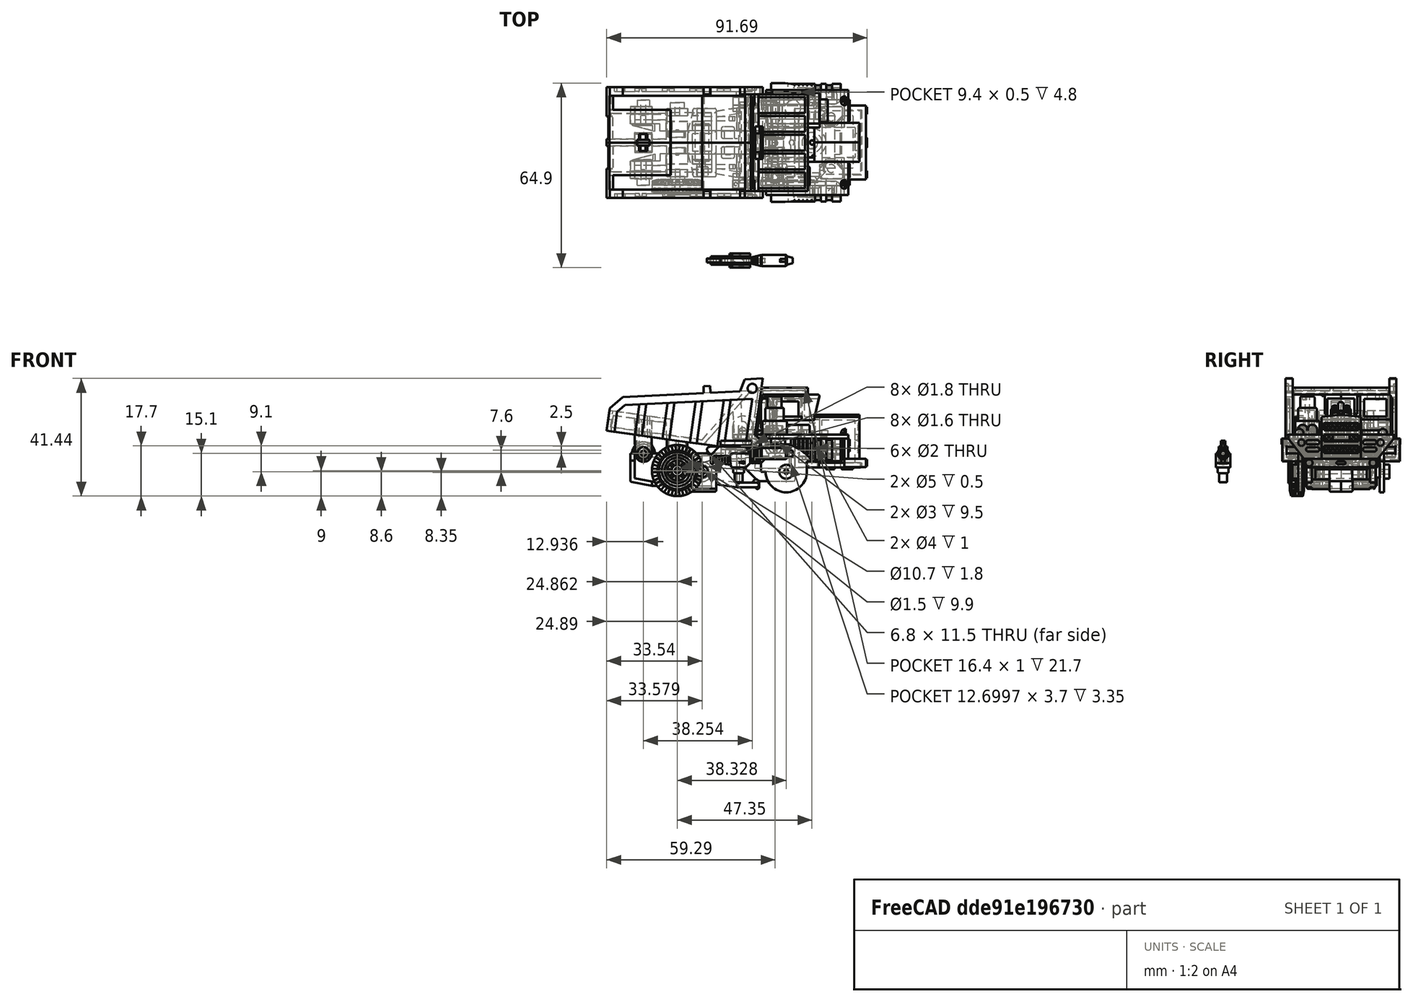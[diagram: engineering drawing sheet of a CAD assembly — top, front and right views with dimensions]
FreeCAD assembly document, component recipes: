
FREECAD ASSEMBLY — COMPONENT RECIPES ("Longhaul")

This assembly document has 21 components, labeled P0..P20 below (a component is one placed body or linked part). 19 of them carry a construction recipe — the FreeCAD feature program that regenerates the part from scratch, quoted from this document or its linked companion documents; the rest are supplied as boundary geometry only. No exploded tour is included for this assembly.
NOTE — document 4 of 4 of this assembly tour. The two overview renders and the header above are repeated from document 1; the component sections below continue where the previous document stopped.
COMPONENT P15 — recipe-attached ("Tire2", modeled in this document).
Construction recipe (the document's own serialized feature program — sketch geometry with constraints, then the solid features built on it; lengths are millimeters unless a unit is written):

FEATURE [Sketcher::SketchObject] Sketch235
  ArcFitTolerance = 1e-06
  AttachmentSupport = -> [XZ_Plane007]
  FullyConstrained = true
  MakeInternals = false
  MapMode = 5
  Placement = pos=(0,0,0) rot=(1,0,0;1.5708rad)
  sketch-geometry (1):
    g0: Circle CenterX=0 CenterY=0 CenterZ=0 NormalX=0 NormalY=0 NormalZ=1 AngleXU=0 Radius=4.5
  constraints (2):
    c: Coincident(g0,g-1)
    c: Diameter(g0) = 9
FEATURE [PartDesign::Pad] Pad145
  Direction = (0,-1,2e-16)
  Length = 5.5
  Length2 = 10
  Placement = pos=(0,0,0) rot=(1,0,0;1.5708rad)
  Profile = -> Sketch235
  ReferenceAxis = -> Sketch235 [N_Axis]
  Refine = true
  Suppressed = false
  Type = 0
FEATURE [Sketcher::SketchObject] Sketch236
  ArcFitTolerance = 1e-06
  AttachmentSupport = -> [Pad145]
  FullyConstrained = true
  MakeInternals = false
  MapMode = 5
  Placement = pos=(0,-5.5,0) rot=(1,0,0;1.5708rad)
  sketch-geometry (1):
    g0: Circle CenterX=0 CenterY=0 CenterZ=0 NormalX=0 NormalY=0 NormalZ=1 AngleXU=0 Radius=3.5
  constraints (2):
    c: Coincident(g0,g-1)
    c: Diameter(g0) = 7
FEATURE [PartDesign::Pocket] Pocket097
  BaseFeature = -> Pad145
  Direction = (0,1,-2e-16)
  Length = 0.5
  Length2 = 5
  Placement = pos=(0,0,0) rot=(1,0,0;1.5708rad)
  Profile = -> Sketch236
  ReferenceAxis = -> Sketch236 [N_Axis]
  Refine = true
  Suppressed = false
  Type = 0
FEATURE [Sketcher::SketchObject] Sketch237
  ArcFitTolerance = 1e-06
  AttachmentSupport = -> [Pocket097]
  FullyConstrained = true
  MakeInternals = false
  MapMode = 5
  Placement = pos=(0,-5,1.5e-15) rot=(1,0,0;1.5708rad)
  sketch-geometry (1):
    g0: Circle CenterX=0 CenterY=0 CenterZ=0 NormalX=0 NormalY=0 NormalZ=1 AngleXU=0 Radius=0.75
  constraints (2):
    c: Coincident(g0,g-1)
    c: Diameter(g0) = 1.5
FEATURE [PartDesign::Pocket] Pocket098
  BaseFeature = -> Pocket097
  Direction = (0,1,-2e-16)
  Length = 5
  Length2 = 5
  Placement = pos=(0,0,0) rot=(1,0,0;1.5708rad)
  Profile = -> Sketch237
  ReferenceAxis = -> Sketch237 [N_Axis]
  Refine = true
  Suppressed = false
  Type = 0
FEATURE [Sketcher::SketchObject] Sketch238
  ArcFitTolerance = 1e-06
  AttachmentSupport = -> [Pocket098]
  FullyConstrained = true
  MakeInternals = false
  MapMode = 5
  Placement = pos=(0,-5,1.5e-15) rot=(1,0,0;1.5708rad)
  sketch-geometry (1):
    g0: Circle CenterX=0 CenterY=0 CenterZ=0 NormalX=0 NormalY=0 NormalZ=1 AngleXU=0 Radius=2
  constraints (2):
    c: Coincident(g0,g-1)
    c: Diameter(g0) = 4
FEATURE [PartDesign::Pocket] Pocket099
  BaseFeature = -> Pocket098
  Direction = (0,1,-2e-16)
  Length = 1.5
  Length2 = 5
  Placement = pos=(0,0,0) rot=(1,0,0;1.5708rad)
  Profile = -> Sketch238
  ReferenceAxis = -> Sketch238 [N_Axis]
  Refine = true
  Suppressed = false
  Type = 0
FEATURE [Sketcher::SketchObject] Sketch239
  ArcFitTolerance = 1e-06
  AttachmentSupport = -> [Pocket099]
  FullyConstrained = true
  MakeInternals = false
  MapMode = 5
  Placement = pos=(0,-5,1.5e-15) rot=(1,0,0;1.5708rad)
  sketch-geometry (12):
    g0: Circle CenterX=0 CenterY=2.75 CenterZ=0 NormalX=0 NormalY=0 NormalZ=1 AngleXU=0 Radius=0.5
    g1: Circle CenterX=2.75 CenterY=0 CenterZ=0 NormalX=0 NormalY=0 NormalZ=1 AngleXU=0 Radius=0.5
    g2: Circle CenterX=0 CenterY=-2.75 CenterZ=0 NormalX=0 NormalY=0 NormalZ=1 AngleXU=0 Radius=0.5
    g3: Circle CenterX=-2.75 CenterY=0 CenterZ=0 NormalX=0 NormalY=0 NormalZ=1 AngleXU=0 Radius=0.5
    g4: Circle CenterX=-1.94454 CenterY=1.94454 CenterZ=0 NormalX=0 NormalY=0 NormalZ=1 AngleXU=0 Radius=0.5
    g5: Circle CenterX=1.94454 CenterY=1.94454 CenterZ=0 NormalX=0 NormalY=0 NormalZ=1 AngleXU=0 Radius=0.5
    g6: Circle CenterX=1.94454 CenterY=-1.94454 CenterZ=0 NormalX=0 NormalY=0 NormalZ=1 AngleXU=0 Radius=0.5
    g7: Circle CenterX=-1.94454 CenterY=-1.94454 CenterZ=0 NormalX=0 NormalY=0 NormalZ=1 AngleXU=0 Radius=0.5
    g8: LineSegment [constr] StartX=0 StartY=0 StartZ=0 EndX=-1.94454 EndY=1.94454 EndZ=0
    g9: LineSegment [constr] StartX=0 StartY=0 StartZ=0 EndX=1.94454 EndY=1.94454 EndZ=0
    g10: LineSegment [constr] StartX=0 StartY=0 StartZ=0 EndX=1.94454 EndY=-1.94454 EndZ=0
    g11: LineSegment [constr] StartX=0 StartY=0 StartZ=0 EndX=-1.94454 EndY=-1.94454 EndZ=0
  constraints (32):
    c: PointOnObject(g0,g-2)
    c: PointOnObject(g1,g-1)
    c: PointOnObject(g2,g-2)
    c: PointOnObject(g3,g-1)
    c: Diameter(g0) = 1
    c: Diameter(g5) = 1
    c: Diameter(g1) = 1
    c: Diameter(g6) = 1
    c: Diameter(g2) = 1
    c: Diameter(g7) = 1
    c: Diameter(g4) = 1
    c: Diameter(g3) = 1
    c: Distance(g-1,g1) = 2.75
    c: Distance(g-1,g0) = 2.75
    c: Distance(g-1,g3) = 2.75
    c: Distance(g-1,g2) = 2.75
    c: Distance(g-1,g6) = 2.75
    c: Distance(g-1,g7) = 2.75
    c: Distance(g-1,g4) = 2.75
    c: Distance(g-1,g5) = 2.75
    c: Coincident(g8,g-1)
    c: Coincident(g8,g4)
    c: Coincident(g9,g8)
    c: Coincident(g9,g5)
    c: Coincident(g10,g8)
    c: Coincident(g10,g6)
    c: Coincident(g11,g8)
    c: Coincident(g11,g7)
    c: Angle(g-2,g8) = 0.785398
    c: Angle(g9,g-2) = 0.785398
    c: Angle(g10,g-1) = 0.785398
    c: Angle(g11,g-1) = 2.35619
FEATURE [PartDesign::Pad] Pad146
  BaseFeature = -> Pocket099
  Direction = (0,-1,2e-16)
  Length = 0.5
  Length2 = 10
  Placement = pos=(0,0,0) rot=(1,0,0;1.5708rad)
  Profile = -> Sketch239
  ReferenceAxis = -> Sketch239 [N_Axis]
  Refine = true
  Suppressed = false
  Type = 0
FEATURE [Sketcher::SketchObject] Sketch240
  ArcFitTolerance = 1e-06
  AttachmentOffset = pos=(0,0,-1) rot=(0,0,1;0rad)
  AttachmentSupport = -> [Pad146]
  ExternalGeometry = -> [Pad146]
  FullyConstrained = true
  MakeInternals = false
  MapMode = 5
  Placement = pos=(0,-4.5,-2e-16) rot=(1,0,0;1.5708rad)
  sketch-geometry (2):
    g0: Circle CenterX=0 CenterY=0 CenterZ=0 NormalX=0 NormalY=0 NormalZ=1 AngleXU=0 Radius=5.5
    g1: Circle CenterX=0 CenterY=0 CenterZ=0 NormalX=0 NormalY=0 NormalZ=1 AngleXU=0 Radius=4.50001
  constraints (4):
    c: Coincident(g0,g-1)
    c: Coincident(g1,g0)
    c: Diameter(g0) = 11
    c: Tangent(g1,g-3)
FEATURE [PartDesign::Pad] Pad147
  BaseFeature = -> Pad146
  Direction = (0,-1,2e-16)
  Length = 4.5
  Length2 = 10
  Placement = pos=(0,0,0) rot=(1,0,0;1.5708rad)
  Profile = -> Sketch240
  ReferenceAxis = -> Sketch240 [N_Axis]
  Refine = true
  Reversed = true
  Suppressed = false
  Type = 0
FEATURE [Sketcher::SketchObject] Sketch241
  ArcFitTolerance = 1e-06
  AttachmentSupport = -> [Pad147]
  ExternalGeometry = -> [Pad147]
  FullyConstrained = true
  MakeInternals = false
  MapMode = 5
  Placement = pos=(0,-5,1.5e-15) rot=(1,0,0;1.5708rad)
  sketch-geometry (2):
    g0: Circle CenterX=0 CenterY=0 CenterZ=0 NormalX=0 NormalY=0 NormalZ=1 AngleXU=0 Radius=5.50001
    g1: Circle CenterX=0 CenterY=0 CenterZ=0 NormalX=0 NormalY=0 NormalZ=1 AngleXU=0 Radius=9
  constraints (4):
    c: Coincident(g0,g-1)
    c: Coincident(g1,g0)
    c: Diameter(g1) = 18
    c: Tangent(g0,g-3)
FEATURE [PartDesign::Pad] Pad148
  BaseFeature = -> Pad147
  Direction = (0,-1,2e-16)
  Length = 5
  Length2 = 10
  Placement = pos=(0,0,0) rot=(1,0,0;1.5708rad)
  Profile = -> Sketch241
  ReferenceAxis = -> Sketch241 [N_Axis]
  Refine = true
  Reversed = true
  Suppressed = false
  Type = 0
FEATURE [Sketcher::SketchObject] Sketch242
  ArcFitTolerance = 1e-06
  AttachmentOffset = pos=(3,0,0) rot=(0,0,1;0rad)
  AttachmentSupport = -> [YZ_Plane007]
  ExternalGeometry = -> [Pad148]
  FullyConstrained = true
  MakeInternals = false
  MapMode = 5
  Placement = pos=(0,3,0) rot=(0.57735,0.57735,0.57735;2.0944rad)
  sketch-geometry (4):
    g0: LineSegment StartX=-8 StartY=6.5 StartZ=0 EndX=-7.5 EndY=5.5 EndZ=0
    g1: LineSegment StartX=-7.5 StartY=5.5 StartZ=0 EndX=-8.5 EndY=5.5 EndZ=0
    g2: LineSegment StartX=-8 StartY=6.5 StartZ=0 EndX=-8.5 EndY=6.5 EndZ=0
    g3: LineSegment StartX=-8.5 StartY=6.5 StartZ=0 EndX=-8.5 EndY=5.5 EndZ=0
  constraints (11):
    c: Coincident(g1,g0)
    c: Horizontal(g1)
    c: Coincident(g0,g-4)
    c: PointOnObject(g0,g-5)
    c: Coincident(g2,g0)
    c: Coincident(g3,g2)
    c: Coincident(g3,g1)
    c: Vertical(g3)
    c: Horizontal(g2)
    c: DistanceY(g0,g0) = 1
    c: DistanceX(g1,g1) = 1
FEATURE [PartDesign::SubtractivePipe] SubtractivePipe
  AuxilleryCurvelinear = true
  AuxillerySpineTangent = false
  BaseFeature = -> Pad148
  Binormal = (0,0,0)
  Mode = 0
  Placement = pos=(0,0,0) rot=(1,0,0;1.5708rad)
  Profile = -> Sketch242
  Refine = true
  Spine = -> Pad148 [Edge6]
  SpineTangent = false
  Suppressed = false
  Transformation = 0
  Transition = 0
FEATURE [PartDesign::Chamfer] Chamfer001
  Angle = 45
  Base = -> SubtractivePipe [Edge10,Edge21]
  BaseFeature = -> SubtractivePipe
  ChamferType = 0
  FlipDirection = false
  Placement = pos=(0,0,0) rot=(1,0,0;1.5708rad)
  Refine = true
  Size = 1.99
  Size2 = 1
  SupportTransform = false
  Suppressed = false
  UseAllEdges = false
FEATURE [Sketcher::SketchObject] Sketch243
  ArcFitTolerance = 1e-06
  AttachmentSupport = -> [Chamfer001]
  ExternalGeometry = -> [Chamfer001]
  FullyConstrained = true
  MakeInternals = false
  MapMode = 5
  Placement = pos=(0,-5,0) rot=(1,0,0;1.5708rad)
  sketch-geometry (120):
    g0: LineSegment [constr] StartX=0 StartY=0 StartZ=0 EndX=-0.706132 EndY=8.97226 EndZ=0
    g1: LineSegment [constr] StartX=0 StartY=0 StartZ=0 EndX=-2.10101 EndY=8.75133 EndZ=0
    g2: LineSegment [constr] StartX=0 StartY=0 StartZ=0 EndX=-3.44415 EndY=8.31492 EndZ=0
    g3: LineSegment [constr] StartX=0 StartY=0 StartZ=0 EndX=-4.70249 EndY=7.67376 EndZ=0
    g4: LineSegment [constr] StartX=0 StartY=0 StartZ=0 EndX=-5.84503 EndY=6.84365 EndZ=0
    g5: LineSegment [constr] StartX=0 StartY=0 StartZ=0 EndX=-6.84365 EndY=5.84503 EndZ=0
    g6: LineSegment [constr] StartX=0 StartY=0 StartZ=0 EndX=-7.67376 EndY=4.70249 EndZ=0
    g7: LineSegment [constr] StartX=0 StartY=0 StartZ=0 EndX=-8.31492 EndY=3.44415 EndZ=0
    g8: LineSegment [constr] StartX=0 StartY=0 StartZ=0 EndX=-8.75133 EndY=2.10101 EndZ=0
    g9: LineSegment [constr] StartX=0 StartY=0 StartZ=0 EndX=-8.97226 EndY=-0.706132 EndZ=0
    g10: LineSegment [constr] StartX=0 StartY=0 StartZ=0 EndX=-8.97226 EndY=0.706132 EndZ=0
    g11: LineSegment [constr] StartX=0 StartY=0 StartZ=0 EndX=-8.75133 EndY=-2.10101 EndZ=0
    g12: LineSegment [constr] StartX=0 StartY=0 StartZ=0 EndX=-8.31492 EndY=-3.44415 EndZ=0
    g13: LineSegment [constr] StartX=0 StartY=0 StartZ=0 EndX=-7.67376 EndY=-4.70249 EndZ=0
    g14: LineSegment [constr] StartX=0 StartY=0 StartZ=0 EndX=-6.84365 EndY=-5.84503 EndZ=0
    g15: LineSegment [constr] StartX=0 StartY=0 StartZ=0 EndX=-5.84503 EndY=-6.84365 EndZ=0
    g16: LineSegment [constr] StartX=0 StartY=0 StartZ=0 EndX=-4.70249 EndY=-7.67376 EndZ=0
    g17: LineSegment [constr] StartX=0 StartY=0 StartZ=0 EndX=-3.44415 EndY=-8.31492 EndZ=0
    g18: LineSegment [constr] StartX=0 StartY=0 StartZ=0 EndX=-2.10101 EndY=-8.75133 EndZ=0
    g19: LineSegment [constr] StartX=0 StartY=0 StartZ=0 EndX=-0.706132 EndY=-8.97226 EndZ=0
    g20: LineSegment [constr] StartX=0 StartY=0 StartZ=0 EndX=0.706132 EndY=-8.97226 EndZ=0
    g21: LineSegment [constr] StartX=0 StartY=0 StartZ=0 EndX=4.70249 EndY=7.67376 EndZ=0
    g22: LineSegment [constr] StartX=0 StartY=0 StartZ=0 EndX=3.44415 EndY=8.31492 EndZ=0
    g23: LineSegment [constr] StartX=0 StartY=0 StartZ=0 EndX=2.10101 EndY=8.75133 EndZ=0
    g24: LineSegment [constr] StartX=0 StartY=0 StartZ=0 EndX=0.706132 EndY=8.97226 EndZ=0
    g25: LineSegment [constr] StartX=0 StartY=0 StartZ=0 EndX=8.97226 EndY=0.706132 EndZ=0
    g26: LineSegment [constr] StartX=0 StartY=0 StartZ=0 EndX=8.97226 EndY=-0.706132 EndZ=0
    g27: LineSegment [constr] StartX=0 StartY=0 StartZ=0 EndX=8.75133 EndY=-2.10101 EndZ=0
    g28: LineSegment [constr] StartX=0 StartY=0 StartZ=0 EndX=8.31492 EndY=-3.44415 EndZ=0
    g29: LineSegment [constr] StartX=0 StartY=0 StartZ=0 EndX=7.67376 EndY=-4.70249 EndZ=0
    g30: LineSegment [constr] StartX=0 StartY=0 StartZ=0 EndX=6.84365 EndY=-5.84503 EndZ=0
    g31: LineSegment [constr] StartX=0 StartY=0 StartZ=0 EndX=5.84503 EndY=-6.84365 EndZ=0
    g32: LineSegment [constr] StartX=0 StartY=0 StartZ=0 EndX=4.70249 EndY=-7.67376 EndZ=0
    g33: LineSegment [constr] StartX=0 StartY=0 StartZ=0 EndX=3.44415 EndY=-8.31492 EndZ=0
    g34: LineSegment [constr] StartX=0 StartY=0 StartZ=0 EndX=2.10101 EndY=-8.75133 EndZ=0
    g35: LineSegment [constr] StartX=0 StartY=0 StartZ=0 EndX=8.75133 EndY=2.10101 EndZ=0
    g36: LineSegment [constr] StartX=0 StartY=0 StartZ=0 EndX=8.31492 EndY=3.44415 EndZ=0
    g37: LineSegment [constr] StartX=0 StartY=0 StartZ=0 EndX=7.67376 EndY=4.70249 EndZ=0
    g38: LineSegment [constr] StartX=0 StartY=0 StartZ=0 EndX=6.84365 EndY=5.84503 EndZ=0
    g39: LineSegment [constr] StartX=0 StartY=0 StartZ=0 EndX=5.84503 EndY=6.84365 EndZ=0
    g40: LineSegment StartX=-0.706132 StartY=8.97226 StartZ=0 EndX=-2.10101 EndY=8.75133 EndZ=0
    g41: LineSegment StartX=-2.10101 StartY=8.75133 StartZ=0 EndX=-1.63645 EndY=6.81631 EndZ=0
    g42: LineSegment StartX=-1.63645 StartY=6.81631 StartZ=0 EndX=-0.549998 EndY=6.98839 EndZ=0
    g43: LineSegment StartX=-0.549998 StartY=6.98839 StartZ=0 EndX=-0.706132 EndY=8.97226 EndZ=0
    g44: LineSegment StartX=-3.44415 StartY=8.31492 StartZ=0 EndX=-4.70249 EndY=7.67376 EndZ=0
    g45: LineSegment StartX=-4.70249 StartY=7.67376 StartZ=0 EndX=-3.66271 EndY=5.97701 EndZ=0
    g46: LineSegment StartX=-3.66271 StartY=5.97701 StartZ=0 EndX=-2.68261 EndY=6.4764 EndZ=0
    g47: LineSegment StartX=-2.68261 StartY=6.4764 StartZ=0 EndX=-3.44415 EndY=8.31492 EndZ=0
    g48: LineSegment StartX=-5.84503 StartY=6.84365 StartZ=0 EndX=-6.84365 EndY=5.84503 EndZ=0
    g49: LineSegment StartX=-6.84365 StartY=5.84503 StartZ=0 EndX=-5.33045 EndY=4.55263 EndZ=0
    g50: LineSegment StartX=-5.33045 StartY=4.55263 StartZ=0 EndX=-4.55263 EndY=5.33045 EndZ=0
    g51: LineSegment StartX=-4.55263 StartY=5.33045 StartZ=0 EndX=-5.84503 EndY=6.84365 EndZ=0
    g52: LineSegment StartX=-7.67376 StartY=4.70249 StartZ=0 EndX=-8.31492 EndY=3.44415 EndZ=0
    g53: LineSegment StartX=-8.31492 StartY=3.44415 StartZ=0 EndX=-6.4764 EndY=2.68261 EndZ=0
    g54: LineSegment StartX=-6.4764 StartY=2.68261 StartZ=0 EndX=-5.97701 EndY=3.66271 EndZ=0
    g55: LineSegment StartX=-5.97701 StartY=3.66271 StartZ=0 EndX=-7.67376 EndY=4.70249 EndZ=0
    g56: LineSegment StartX=-8.75133 StartY=2.10101 StartZ=0 EndX=-8.97226 EndY=0.706132 EndZ=0
    g57: LineSegment StartX=-8.97226 StartY=0.706132 StartZ=0 EndX=-6.98839 EndY=0.549998 EndZ=0
    g58: LineSegment StartX=-6.98839 StartY=0.549998 StartZ=0 EndX=-6.81631 EndY=1.63645 EndZ=0
    g59: LineSegment StartX=-6.81631 StartY=1.63645 StartZ=0 EndX=-8.75133 EndY=2.10101 EndZ=0
    g60: LineSegment StartX=-8.97226 StartY=-0.706132 StartZ=0 EndX=-8.75133 EndY=-2.10101 EndZ=0
    g61: LineSegment StartX=-8.75133 StartY=-2.10101 StartZ=0 EndX=-6.81631 EndY=-1.63645 EndZ=0
    g62: LineSegment StartX=-6.81631 StartY=-1.63645 StartZ=0 EndX=-6.98839 EndY=-0.549998 EndZ=0
    g63: LineSegment StartX=-6.98839 StartY=-0.549998 StartZ=0 EndX=-8.97226 EndY=-0.706132 EndZ=0
    g64: LineSegment StartX=-8.31492 StartY=-3.44415 StartZ=0 EndX=-7.67376 EndY=-4.70249 EndZ=0
    g65: LineSegment StartX=-7.67376 StartY=-4.70249 StartZ=0 EndX=-5.97701 EndY=-3.66271 EndZ=0
    g66: LineSegment StartX=-5.97701 StartY=-3.66271 StartZ=0 EndX=-6.4764 EndY=-2.68261 EndZ=0
    g67: LineSegment StartX=-6.4764 StartY=-2.68261 StartZ=0 EndX=-8.31492 EndY=-3.44415 EndZ=0
    g68: LineSegment StartX=-6.84365 StartY=-5.84503 StartZ=0 EndX=-5.84503 EndY=-6.84365 EndZ=0
    g69: LineSegment StartX=-5.84503 StartY=-6.84365 StartZ=0 EndX=-4.55263 EndY=-5.33045 EndZ=0
    g70: LineSegment StartX=-4.55263 StartY=-5.33045 StartZ=0 EndX=-5.33045 EndY=-4.55263 EndZ=0
    g71: LineSegment StartX=-5.33045 StartY=-4.55263 StartZ=0 EndX=-6.84365 EndY=-5.84503 EndZ=0
    g72: LineSegment StartX=-4.70249 StartY=-7.67376 StartZ=0 EndX=-3.44415 EndY=-8.31492 EndZ=0
    g73: LineSegment StartX=-3.44415 StartY=-8.31492 StartZ=0 EndX=-2.68261 EndY=-6.4764 EndZ=0
    g74: LineSegment StartX=-2.68261 StartY=-6.4764 StartZ=0 EndX=-3.66271 EndY=-5.97701 EndZ=0
    g75: LineSegment StartX=-3.66271 StartY=-5.97701 StartZ=0 EndX=-4.70249 EndY=-7.67376 EndZ=0
    g76: LineSegment StartX=-2.10101 StartY=-8.75133 StartZ=0 EndX=-1.63645 EndY=-6.81631 EndZ=0
    g77: LineSegment StartX=-1.63645 StartY=-6.81631 StartZ=0 EndX=-0.549998 EndY=-6.98839 EndZ=0
    g78: LineSegment StartX=-0.549998 StartY=-6.98839 StartZ=0 EndX=-0.706132 EndY=-8.97226 EndZ=0
    g79: LineSegment StartX=-0.706132 StartY=-8.97226 StartZ=0 EndX=-2.10101 EndY=-8.75133 EndZ=0
    g80: LineSegment StartX=0.706132 StartY=-8.97226 StartZ=0 EndX=2.10101 EndY=-8.75133 EndZ=0
    g81: LineSegment StartX=2.10101 StartY=-8.75133 StartZ=0 EndX=1.63645 EndY=-6.81631 EndZ=0
    g82: LineSegment StartX=1.63645 StartY=-6.81631 StartZ=0 EndX=0.549998 EndY=-6.98839 EndZ=0
    g83: LineSegment StartX=0.549998 StartY=-6.98839 StartZ=0 EndX=0.706132 EndY=-8.97226 EndZ=0
    g84: LineSegment StartX=3.44415 StartY=-8.31492 StartZ=0 EndX=4.70249 EndY=-7.67376 EndZ=0
    g85: LineSegment StartX=4.70249 StartY=-7.67376 StartZ=0 EndX=3.66271 EndY=-5.97701 EndZ=0
    g86: LineSegment StartX=3.66271 StartY=-5.97701 StartZ=0 EndX=2.68261 EndY=-6.4764 EndZ=0
    g87: LineSegment StartX=2.68261 StartY=-6.4764 StartZ=0 EndX=3.44415 EndY=-8.31492 EndZ=0
    g88: LineSegment StartX=5.84503 StartY=-6.84365 StartZ=0 EndX=6.84365 EndY=-5.84503 EndZ=0
    g89: LineSegment StartX=6.84365 StartY=-5.84503 StartZ=0 EndX=5.33045 EndY=-4.55263 EndZ=0
    g90: LineSegment StartX=5.33045 StartY=-4.55263 StartZ=0 EndX=4.55263 EndY=-5.33045 EndZ=0
    g91: LineSegment StartX=5.84503 StartY=-6.84365 StartZ=0 EndX=4.55263 EndY=-5.33045 EndZ=0
    g92: LineSegment StartX=7.67376 StartY=-4.70249 StartZ=0 EndX=5.97701 EndY=-3.66271 EndZ=0
    g93: LineSegment StartX=7.67376 StartY=-4.70249 StartZ=0 EndX=8.31492 EndY=-3.44415 EndZ=0
    g94: LineSegment StartX=8.31492 StartY=-3.44415 StartZ=0 EndX=6.4764 EndY=-2.68261 EndZ=0
    g95: LineSegment StartX=6.4764 StartY=-2.68261 StartZ=0 EndX=5.97701 EndY=-3.66271 EndZ=0
    g96: LineSegment StartX=8.75133 StartY=-2.10101 StartZ=0 EndX=8.97226 EndY=-0.706132 EndZ=0
    g97: LineSegment StartX=8.97226 StartY=-0.706132 StartZ=0 EndX=6.98839 EndY=-0.549998 EndZ=0
    g98: LineSegment StartX=6.98839 StartY=-0.549998 StartZ=0 EndX=6.81631 EndY=-1.63645 EndZ=0
    g99: LineSegment StartX=8.75133 StartY=-2.10101 StartZ=0 EndX=6.81631 EndY=-1.63645 EndZ=0
    g100: LineSegment StartX=8.97226 StartY=0.706132 StartZ=0 EndX=8.75133 EndY=2.10101 EndZ=0
    g101: LineSegment StartX=8.75133 StartY=2.10101 StartZ=0 EndX=6.81631 EndY=1.63645 EndZ=0
    g102: LineSegment StartX=8.97226 StartY=0.706132 StartZ=0 EndX=6.98839 EndY=0.549998 EndZ=0
    g103: LineSegment StartX=6.98839 StartY=0.549998 StartZ=0 EndX=6.81631 EndY=1.63645 EndZ=0
    g104: LineSegment StartX=8.31492 StartY=3.44415 StartZ=0 EndX=7.67376 EndY=4.70249 EndZ=0
    g105: LineSegment StartX=7.67376 StartY=4.70249 StartZ=0 EndX=5.97701 EndY=3.66271 EndZ=0
    g106: LineSegment StartX=5.97701 StartY=3.66271 StartZ=0 EndX=6.4764 EndY=2.68261 EndZ=0
    g107: LineSegment StartX=6.4764 StartY=2.68261 StartZ=0 EndX=8.31492 EndY=3.44415 EndZ=0
    g108: LineSegment StartX=6.84365 StartY=5.84503 StartZ=0 EndX=5.84503 EndY=6.84365 EndZ=0
    g109: LineSegment StartX=5.84503 StartY=6.84365 StartZ=0 EndX=4.55263 EndY=5.33045 EndZ=0
    g110: LineSegment StartX=6.84365 StartY=5.84503 StartZ=0 EndX=5.33045 EndY=4.55263 EndZ=0
    g111: LineSegment StartX=5.33045 StartY=4.55263 StartZ=0 EndX=4.55263 EndY=5.33045 EndZ=0
    g112: LineSegment StartX=4.70249 StartY=7.67376 StartZ=0 EndX=3.66271 EndY=5.97701 EndZ=0
    g113: LineSegment StartX=4.70249 StartY=7.67376 StartZ=0 EndX=3.44415 EndY=8.31492 EndZ=0
    g114: LineSegment StartX=3.44415 StartY=8.31492 StartZ=0 EndX=2.68261 EndY=6.4764 EndZ=0
    g115: LineSegment StartX=2.68261 StartY=6.4764 StartZ=0 EndX=3.66271 EndY=5.97701 EndZ=0
    g116: LineSegment StartX=0.706132 StartY=8.97226 StartZ=0 EndX=2.10101 EndY=8.75133 EndZ=0
    g117: LineSegment StartX=2.10101 StartY=8.75133 StartZ=0 EndX=1.63645 EndY=6.81631 EndZ=0
    g118: LineSegment StartX=1.63645 StartY=6.81631 StartZ=0 EndX=0.549998 EndY=6.98839 EndZ=0
    g119: LineSegment StartX=0.549998 StartY=6.98839 StartZ=0 EndX=0.706132 EndY=8.97226 EndZ=0
  constraints (320):
    c: Coincident(g0,g-1)
    c: PointOnObject(g0,g-3)
    c: Coincident(g1,g0)
    c: PointOnObject(g1,g-3)
    c: Coincident(g2,g0)
    c: PointOnObject(g2,g-3)
    c: Coincident(g3,g0)
    c: PointOnObject(g3,g-3)
    c: Coincident(g4,g0)
    c: PointOnObject(g4,g-3)
    c: Coincident(g5,g0)
    c: PointOnObject(g5,g-3)
    c: Angle(g-2,g0) = 0.0785398
    c: Angle(g0,g1) = 0.15708
    c: Angle(g1,g2) = 0.15708
    c: Angle(g2,g3) = 0.15708
    c: Angle(g3,g4) = 0.15708
    c: Angle(g4,g5) = 0.15708
    c: Coincident(g6,g0)
    c: PointOnObject(g6,g-3)
    c: Coincident(g7,g0)
    c: PointOnObject(g7,g-3)
    c: Coincident(g8,g0)
    c: PointOnObject(g8,g-3)
    c: Coincident(g9,g0)
    c: PointOnObject(g9,g-3)
    c: Coincident(g10,g0)
    c: PointOnObject(g10,g-3)
    c: Coincident(g11,g0)
    c: PointOnObject(g11,g-3)
    c: Coincident(g12,g0)
    c: PointOnObject(g12,g-3)
    c: Coincident(g13,g0)
    c: PointOnObject(g13,g-3)
    c: Coincident(g14,g0)
    c: PointOnObject(g14,g-3)
    c: Angle(g5,g6) = 0.15708
    c: Angle(g6,g7) = 0.15708
    c: Angle(g7,g8) = 0.15708
    c: Angle(g8,g10) = 0.15708
    c: Angle(g10,g9) = 0.15708
    c: Angle(g9,g11) = 0.15708
    c: Angle(g11,g12) = 0.15708
    c: Angle(g12,g13) = 0.15708
    c: Angle(g13,g14) = 0.15708
    c: Coincident(g15,g0)
    c: PointOnObject(g15,g-3)
    c: Coincident(g16,g0)
    c: PointOnObject(g16,g-3)
    c: Coincident(g17,g0)
    c: PointOnObject(g17,g-3)
    c: Coincident(g18,g0)
    c: PointOnObject(g18,g-3)
    c: Coincident(g19,g0)
    c: PointOnObject(g19,g-3)
    c: Coincident(g20,g0)
    c: PointOnObject(g20,g-3)
    c: Coincident(g21,g0)
    c: PointOnObject(g21,g-3)
    c: Coincident(g22,g0)
    c: PointOnObject(g22,g-3)
    c: Coincident(g23,g0)
    c: PointOnObject(g23,g-3)
    c: Coincident(g24,g0)
    c: PointOnObject(g24,g-3)
    c: Angle(g14,g15) = 0.15708
    c: Angle(g15,g16) = 0.15708
    c: Angle(g16,g17) = 0.15708
    c: Angle(g17,g18) = 0.15708
    c: Angle(g18,g19) = 0.15708
    c: Angle(g19,g20) = 0.15708
    c: Angle(g24,g0) = 0.15708
    c: Angle(g23,g24) = 0.15708
    c: Angle(g22,g23) = 0.15708
    c: Angle(g21,g22) = 0.15708
    c: Coincident(g25,g0)
    c: PointOnObject(g25,g-3)
    c: Coincident(g26,g0)
    c: PointOnObject(g26,g-3)
    c: Coincident(g27,g0)
    c: PointOnObject(g27,g-3)
    c: Coincident(g28,g0)
    c: PointOnObject(g28,g-3)
    c: Coincident(g29,g0)
    c: PointOnObject(g29,g-3)
    c: Coincident(g30,g0)
    c: PointOnObject(g30,g-3)
    c: Coincident(g31,g0)
    c: PointOnObject(g31,g-3)
    c: Coincident(g32,g0)
    c: PointOnObject(g32,g-3)
    c: Coincident(g33,g0)
    c: PointOnObject(g33,g-3)
    c: Coincident(g34,g0)
    c: PointOnObject(g34,g-3)
    c: Angle(g20,g34) = 0.15708
    c: Angle(g34,g33) = 0.15708
    c: Angle(g33,g32) = 0.15708
    c: Angle(g32,g31) = 0.15708
    c: Angle(g31,g30) = 0.15708
    c: Angle(g30,g29) = 0.15708
    c: Angle(g29,g28) = 0.15708
    c: Angle(g28,g27) = 0.15708
    c: Angle(g27,g26) = 0.15708
    c: Angle(g26,g25) = 0.15708
    c: Coincident(g35,g0)
    c: PointOnObject(g35,g-3)
    c: Coincident(g36,g0)
    c: PointOnObject(g36,g-3)
    c: Coincident(g37,g0)
    c: PointOnObject(g37,g-3)
    c: Coincident(g38,g0)
    c: PointOnObject(g38,g-3)
    c: Coincident(g39,g0)
    c: PointOnObject(g39,g-3)
    c: Angle(g25,g35) = 0.15708
    c: Angle(g35,g36) = 0.15708
    c: Angle(g36,g37) = 0.15708
    c: Angle(g37,g38) = 0.15708
    c: Angle(g38,g39) = 0.15708
    c: Coincident(g40,g0)
    c: Coincident(g40,g1)
    c: Coincident(g41,g1)
    c: PointOnObject(g41,g1)
    c: Coincident(g42,g41)
    c: PointOnObject(g42,g0)
    c: Coincident(g43,g42)
    c: Coincident(g43,g0)
    c: PointOnObject(g42,g-4)
    c: PointOnObject(g41,g-4)
    c: Coincident(g44,g2)
    c: Coincident(g45,g44)
    c: PointOnObject(g45,g3)
    c: Coincident(g46,g45)
    c: PointOnObject(g46,g2)
    c: Coincident(g47,g46)
    c: Coincident(g47,g2)
    c: Coincident(g48,g4)
    c: PointOnObject(g49,g5)
    c: Coincident(g50,g49)
    c: PointOnObject(g50,g4)
    c: Coincident(g51,g50)
    c: Coincident(g51,g4)
    c: Coincident(g52,g6)
    c: PointOnObject(g53,g7)
    c: Coincident(g54,g53)
    c: PointOnObject(g54,g6)
    c: Coincident(g55,g54)
    c: Coincident(g55,g6)
    c: Coincident(g56,g8)
    c: PointOnObject(g57,g10)
    c: Coincident(g58,g57)
    c: PointOnObject(g58,g8)
    c: Coincident(g59,g58)
    c: Coincident(g59,g56)
    c: Coincident(g60,g11)
    c: PointOnObject(g61,g11)
    c: Coincident(g62,g61)
    c: PointOnObject(g62,g9)
    c: Coincident(g63,g60)
    c: Coincident(g64,g12)
    c: Coincident(g64,g13)
    c: PointOnObject(g65,g13)
    c: Coincident(g66,g65)
    c: PointOnObject(g66,g12)
    c: Coincident(g67,g66)
    c: Coincident(g67,g12)
    c: Coincident(g68,g14)
    c: Coincident(g68,g15)
    c: Coincident(g69,g68)
    c: PointOnObject(g69,g15)
    c: Coincident(g70,g69)
    c: PointOnObject(g70,g14)
    c: Coincident(g71,g70)
    c: Coincident(g71,g68)
    c: Coincident(g72,g16)
    c: Coincident(g72,g17)
    c: Coincident(g73,g17)
    c: PointOnObject(g73,g17)
    c: Coincident(g74,g73)
    c: PointOnObject(g74,g16)
    c: Coincident(g75,g74)
    c: Coincident(g75,g16)
    c: Coincident(g76,g18)
    c: PointOnObject(g76,g18)
    c: Coincident(g77,g76)
    c: PointOnObject(g77,g19)
    c: Coincident(g78,g77)
    c: Coincident(g78,g19)
    c: Coincident(g79,g78)
    c: Coincident(g79,g18)
    c: PointOnObject(g46,g-4)
    c: PointOnObject(g45,g-4)
    c: Coincident(g44,g3)
    c: PointOnObject(g50,g-4)
    c: PointOnObject(g49,g-4)
    c: Coincident(g48,g5)
    c: Coincident(g49,g5)
    c: PointOnObject(g54,g-4)
    c: PointOnObject(g53,g-4)
    c: Coincident(g53,g52)
    c: Coincident(g53,g7)
    c: PointOnObject(g58,g-4)
    c: PointOnObject(g57,g-4)
    c: Coincident(g57,g56)
    c: Coincident(g56,g10)
    c: Coincident(g60,g9)
    c: Coincident(g61,g11)
    c: PointOnObject(g61,g-4)
    c: Coincident(g63,g62)
    c: PointOnObject(g62,g-4)
    c: PointOnObject(g66,g-4)
    c: PointOnObject(g65,g-4)
    c: Coincident(g65,g13)
    c: PointOnObject(g70,g-4)
    c: PointOnObject(g69,g-4)
    c: PointOnObject(g73,g-4)
    c: PointOnObject(g74,g-4)
    c: PointOnObject(g76,g-4)
    c: PointOnObject(g77,g-4)
    c: Coincident(g80,g20)
    c: Coincident(g80,g34)
    c: Coincident(g81,g34)
    c: PointOnObject(g81,g34)
    c: Coincident(g82,g81)
    c: PointOnObject(g82,g20)
    c: Coincident(g83,g82)
    c: Coincident(g83,g20)
    c: Coincident(g84,g33)
    c: Coincident(g84,g32)
    c: Coincident(g85,g32)
    c: PointOnObject(g85,g32)
    c: Coincident(g86,g85)
    c: PointOnObject(g86,g33)
    c: Coincident(g87,g86)
    c: Coincident(g87,g33)
    c: Coincident(g88,g31)
    c: Coincident(g88,g30)
    c: Coincident(g89,g30)
    c: PointOnObject(g89,g30)
    c: Coincident(g90,g89)
    c: PointOnObject(g90,g31)
    c: Coincident(g91,g31)
    c: Coincident(g91,g90)
    c: Coincident(g92,g29)
    c: PointOnObject(g92,g29)
    c: Coincident(g93,g29)
    c: Coincident(g93,g28)
    c: Coincident(g94,g28)
    c: PointOnObject(g94,g28)
    c: Coincident(g95,g94)
    c: Coincident(g95,g92)
    c: Coincident(g96,g27)
    c: Coincident(g96,g26)
    c: Coincident(g97,g26)
    c: PointOnObject(g97,g26)
    c: Coincident(g98,g97)
    c: PointOnObject(g98,g27)
    c: Coincident(g99,g96)
    c: Coincident(g99,g98)
    c: Coincident(g100,g25)
    c: Coincident(g100,g35)
    c: Coincident(g101,g35)
    c: PointOnObject(g101,g35)
    c: Coincident(g102,g100)
    c: PointOnObject(g102,g25)
    c: Coincident(g103,g102)
    c: Coincident(g103,g101)
    c: Coincident(g104,g36)
    c: Coincident(g104,g37)
    c: Coincident(g105,g37)
    c: PointOnObject(g105,g37)
    c: Coincident(g106,g105)
    c: PointOnObject(g106,g36)
    c: Coincident(g107,g106)
    c: Coincident(g107,g36)
    c: Coincident(g108,g38)
    c: Coincident(g108,g39)
    c: Coincident(g109,g108)
    c: PointOnObject(g109,g39)
    c: Coincident(g110,g38)
    c: PointOnObject(g110,g38)
    c: Coincident(g111,g110)
    c: Coincident(g111,g109)
    c: Coincident(g112,g21)
    c: PointOnObject(g112,g21)
    c: Coincident(g113,g21)
    c: Coincident(g113,g22)
    c: Coincident(g114,g22)
    c: PointOnObject(g114,g22)
    c: Coincident(g115,g114)
    c: Coincident(g115,g112)
    c: Coincident(g116,g24)
    c: Coincident(g116,g23)
    c: Coincident(g117,g23)
    c: PointOnObject(g117,g23)
    c: Coincident(g118,g117)
    c: PointOnObject(g118,g24)
    c: Coincident(g119,g118)
    c: Coincident(g119,g24)
    c: PointOnObject(g118,g-4)
    c: PointOnObject(g117,g-4)
    c: PointOnObject(g114,g-4)
    c: PointOnObject(g112,g-4)
    c: PointOnObject(g109,g-4)
    c: PointOnObject(g110,g-4)
    c: PointOnObject(g105,g-4)
    c: PointOnObject(g106,g-4)
    c: PointOnObject(g101,g-4)
    c: PointOnObject(g102,g-4)
    c: PointOnObject(g97,g-4)
    c: PointOnObject(g98,g-4)
    c: PointOnObject(g94,g-4)
    c: PointOnObject(g92,g-4)
    c: PointOnObject(g89,g-4)
    c: PointOnObject(g90,g-4)
    c: PointOnObject(g85,g-4)
    c: PointOnObject(g86,g-4)
    c: PointOnObject(g81,g-4)
    c: PointOnObject(g82,g-4)
FEATURE [PartDesign::Pad] Pad149
  BaseFeature = -> Chamfer001
  Direction = (0,-1,2e-16)
  Length = 2
  Length2 = 10
  Placement = pos=(0,0,0) rot=(1,0,0;1.5708rad)
  Profile = -> Sketch243
  ReferenceAxis = -> Sketch243 [N_Axis]
  Refine = true
  Reversed = true
  Suppressed = false
  Type = 0
FEATURE [Sketcher::SketchObject] Sketch244
  ArcFitTolerance = 1e-06
  AttachmentSupport = -> [Pad149]
  ExternalGeometry = -> [Pad149]
  FullyConstrained = true
  MakeInternals = false
  MapMode = 5
  Placement = pos=(2e-16,0,0) rot=(0.734323,0,0.678801;3.14159rad)
  sketch-geometry (3):
    g0: LineSegment StartX=-7.01 StartY=5 StartZ=0 EndX=-9 EndY=5 EndZ=0
    g1: LineSegment StartX=-9 StartY=5 StartZ=0 EndX=-9 EndY=4.5 EndZ=0
    g2: LineSegment StartX=-9 StartY=4.5 StartZ=0 EndX=-7.01 EndY=5 EndZ=0
  constraints (7):
    c: Coincident(g0,g-3)
    c: Coincident(g0,g-4)
    c: Coincident(g1,g0)
    c: PointOnObject(g1,g-4)
    c: Coincident(g2,g1)
    c: Coincident(g2,g0)
    c: DistanceY(g1,g1) = 0.5
FEATURE [PartDesign::SubtractivePipe] SubtractivePipe001
  AuxilleryCurvelinear = true
  AuxillerySpineTangent = false
  BaseFeature = -> Pad149
  Binormal = (0,0,0)
  Mode = 0
  Placement = pos=(0,0,0) rot=(1,0,0;1.5708rad)
  Profile = -> Sketch244
  Refine = true
  Spine = -> Pad149 [Edge3]
  SpineTangent = false
  Suppressed = false
  Transformation = 0
  Transition = 0
FEATURE [Sketcher::SketchObject] Sketch245
  ArcFitTolerance = 1e-06
  AttachmentSupport = -> [SubtractivePipe001]
  FullyConstrained = true
  MakeInternals = false
  MapMode = 5
  Placement = pos=(0,-7.1e-15,0) rot=(-1,0,0;1.5708rad)
  sketch-geometry (1):
    g0: Circle CenterX=0 CenterY=0 CenterZ=0 NormalX=0 NormalY=0 NormalZ=1 AngleXU=0 Radius=2.7
  constraints (2):
    c: Coincident(g0,g-1)
    c: Diameter(g0) = 5.4
FEATURE [PartDesign::Pocket] Pocket100
  BaseFeature = -> SubtractivePipe001
  Direction = (0,-1,-2e-16)
  Length = 1.8
  Length2 = 5
  Placement = pos=(0,0,0) rot=(1,0,0;1.5708rad)
  Profile = -> Sketch245
  ReferenceAxis = -> Sketch245 [N_Axis]
  Refine = true
  Suppressed = false
  Type = 0
FEATURE [Sketcher::SketchObject] Sketch246
  ArcFitTolerance = 1e-06
  AttachmentSupport = -> [Pocket100]
  FullyConstrained = true
  MakeInternals = false
  MapMode = 5
  Placement = pos=(0,-7.1e-15,0) rot=(-1,0,0;1.5708rad)
  sketch-geometry (2):
    g0: Circle CenterX=0 CenterY=0 CenterZ=0 NormalX=0 NormalY=0 NormalZ=1 AngleXU=0 Radius=4
    g1: Circle CenterX=0 CenterY=0 CenterZ=0 NormalX=0 NormalY=0 NormalZ=1 AngleXU=0 Radius=5.35
  constraints (4):
    c: Coincident(g0,g-1)
    c: Coincident(g1,g0)
    c: Diameter(g0) = 8
    c: Diameter(g1) = 10.7
FEATURE [PartDesign::Pocket] Pocket101
  BaseFeature = -> Pocket100
  Direction = (0,-1,-2e-16)
  Length = 1.8
  Length2 = 5
  Placement = pos=(0,0,0) rot=(1,0,0;1.5708rad)
  Profile = -> Sketch246
  ReferenceAxis = -> Sketch246 [N_Axis]
  Refine = true
  Suppressed = false
  Type = 0
FEATURE [Sketcher::SketchObject] Sketch247
  ArcFitTolerance = 1e-06
  AttachmentSupport = -> [Pocket101]
  ExternalGeometry = -> [Pocket101]
  FullyConstrained = true
  MakeInternals = false
  MapMode = 5
  Placement = pos=(0,-7.1e-15,0) rot=(-1,0,0;1.5708rad)
  sketch-geometry (120):
    g0: LineSegment [constr] StartX=0 StartY=0 StartZ=0 EndX=0.706132 EndY=8.97226 EndZ=0
    g1: LineSegment [constr] StartX=0 StartY=0 StartZ=0 EndX=2.10101 EndY=8.75133 EndZ=0
    g2: LineSegment [constr] StartX=0 StartY=0 StartZ=0 EndX=3.44415 EndY=8.31492 EndZ=0
    g3: LineSegment [constr] StartX=0 StartY=0 StartZ=0 EndX=4.70249 EndY=7.67376 EndZ=0
    g4: LineSegment [constr] StartX=0 StartY=0 StartZ=0 EndX=5.84503 EndY=6.84365 EndZ=0
    g5: LineSegment [constr] StartX=0 StartY=0 StartZ=0 EndX=6.84365 EndY=5.84503 EndZ=0
    g6: LineSegment [constr] StartX=0 StartY=0 StartZ=0 EndX=7.67376 EndY=4.70249 EndZ=0
    g7: LineSegment [constr] StartX=0 StartY=0 StartZ=0 EndX=8.31492 EndY=3.44415 EndZ=0
    g8: LineSegment [constr] StartX=0 StartY=0 StartZ=0 EndX=8.75133 EndY=2.10101 EndZ=0
    g9: LineSegment [constr] StartX=0 StartY=0 StartZ=0 EndX=8.97226 EndY=0.706132 EndZ=0
    g10: LineSegment [constr] StartX=0 StartY=0 StartZ=0 EndX=8.97226 EndY=-0.706132 EndZ=0
    g11: LineSegment [constr] StartX=0 StartY=0 StartZ=0 EndX=8.75133 EndY=-2.10101 EndZ=0
    g12: LineSegment [constr] StartX=0 StartY=0 StartZ=0 EndX=8.31492 EndY=-3.44415 EndZ=0
    g13: LineSegment [constr] StartX=0 StartY=0 StartZ=0 EndX=7.67376 EndY=-4.70249 EndZ=0
    g14: LineSegment [constr] StartX=0 StartY=0 StartZ=0 EndX=6.84365 EndY=-5.84503 EndZ=0
    g15: LineSegment [constr] StartX=0 StartY=0 StartZ=0 EndX=5.84503 EndY=-6.84365 EndZ=0
    g16: LineSegment [constr] StartX=0 StartY=0 StartZ=0 EndX=4.70249 EndY=-7.67376 EndZ=0
    g17: LineSegment [constr] StartX=0 StartY=0 StartZ=0 EndX=3.44415 EndY=-8.31492 EndZ=0
    g18: LineSegment [constr] StartX=0 StartY=0 StartZ=0 EndX=2.10101 EndY=-8.75133 EndZ=0
    g19: LineSegment [constr] StartX=0 StartY=0 StartZ=0 EndX=0.706132 EndY=-8.97226 EndZ=0
    g20: LineSegment [constr] StartX=0 StartY=0 StartZ=0 EndX=-0.706132 EndY=-8.97226 EndZ=0
    g21: LineSegment [constr] StartX=0 StartY=0 StartZ=0 EndX=-6.84365 EndY=5.84503 EndZ=0
    g22: LineSegment [constr] StartX=0 StartY=0 StartZ=0 EndX=-5.84503 EndY=6.84365 EndZ=0
    g23: LineSegment [constr] StartX=0 StartY=0 StartZ=0 EndX=-4.70249 EndY=7.67376 EndZ=0
    g24: LineSegment [constr] StartX=0 StartY=0 StartZ=0 EndX=-3.44415 EndY=8.31492 EndZ=0
    g25: LineSegment [constr] StartX=0 StartY=0 StartZ=0 EndX=-2.10101 EndY=8.75133 EndZ=0
    g26: LineSegment [constr] StartX=0 StartY=0 StartZ=0 EndX=-8.75133 EndY=2.10101 EndZ=0
    g27: LineSegment [constr] StartX=0 StartY=0 StartZ=0 EndX=-8.97226 EndY=0.706132 EndZ=0
    g28: LineSegment [constr] StartX=0 StartY=0 StartZ=0 EndX=-8.97226 EndY=-0.706132 EndZ=0
    g29: LineSegment [constr] StartX=0 StartY=0 StartZ=0 EndX=-8.75133 EndY=-2.10101 EndZ=0
    g30: LineSegment [constr] StartX=0 StartY=0 StartZ=0 EndX=-8.31492 EndY=-3.44415 EndZ=0
    g31: LineSegment [constr] StartX=0 StartY=0 StartZ=0 EndX=-7.67376 EndY=-4.70249 EndZ=0
    g32: LineSegment [constr] StartX=0 StartY=0 StartZ=0 EndX=-6.84365 EndY=-5.84503 EndZ=0
    g33: LineSegment [constr] StartX=0 StartY=0 StartZ=0 EndX=-5.84503 EndY=-6.84365 EndZ=0
    g34: LineSegment [constr] StartX=0 StartY=0 StartZ=0 EndX=-4.70249 EndY=-7.67376 EndZ=0
    g35: LineSegment [constr] StartX=0 StartY=0 StartZ=0 EndX=-3.44415 EndY=-8.31492 EndZ=0
    g36: LineSegment [constr] StartX=0 StartY=0 StartZ=0 EndX=-2.10101 EndY=-8.75133 EndZ=0
    g37: LineSegment [constr] StartX=0 StartY=0 StartZ=0 EndX=-8.31492 EndY=3.44415 EndZ=0
    g38: LineSegment [constr] StartX=0 StartY=0 StartZ=0 EndX=-7.67376 EndY=4.70249 EndZ=0
    g39: LineSegment [constr] StartX=0 StartY=0 StartZ=0 EndX=-0.706132 EndY=8.97226 EndZ=0
    g40: LineSegment StartX=0.706132 StartY=8.97226 StartZ=0 EndX=-0.706132 EndY=8.97226 EndZ=0
    g41: LineSegment StartX=-0.706132 StartY=8.97226 StartZ=0 EndX=-0.549998 EndY=6.98839 EndZ=0
    g42: LineSegment StartX=-0.549998 StartY=6.98839 StartZ=0 EndX=0.549998 EndY=6.98839 EndZ=0
    g43: LineSegment StartX=0.549998 StartY=6.98839 StartZ=0 EndX=0.706132 EndY=8.97226 EndZ=0
    g44: LineSegment StartX=2.10101 StartY=8.75133 StartZ=0 EndX=1.63645 EndY=6.81631 EndZ=0
    g45: LineSegment StartX=1.63645 StartY=6.81631 StartZ=0 EndX=2.68261 EndY=6.4764 EndZ=0
    g46: LineSegment StartX=2.68261 StartY=6.4764 StartZ=0 EndX=3.44415 EndY=8.31492 EndZ=0
    g47: LineSegment StartX=3.44415 StartY=8.31492 StartZ=0 EndX=2.10101 EndY=8.75133 EndZ=0
    g48: LineSegment StartX=4.70249 StartY=7.67376 StartZ=0 EndX=5.84503 EndY=6.84365 EndZ=0
    g49: LineSegment StartX=5.84503 StartY=6.84365 StartZ=0 EndX=4.55263 EndY=5.33045 EndZ=0
    g50: LineSegment StartX=4.55263 StartY=5.33045 StartZ=0 EndX=3.66271 EndY=5.97701 EndZ=0
    g51: LineSegment StartX=3.66271 StartY=5.97701 StartZ=0 EndX=4.70249 EndY=7.67376 EndZ=0
    g52: LineSegment StartX=6.84365 StartY=5.84503 StartZ=0 EndX=7.67376 EndY=4.70249 EndZ=0
    g53: LineSegment StartX=7.67376 StartY=4.70249 StartZ=0 EndX=5.97701 EndY=3.66271 EndZ=0
    g54: LineSegment StartX=5.97701 StartY=3.66271 StartZ=0 EndX=5.33045 EndY=4.55263 EndZ=0
    g55: LineSegment StartX=5.33045 StartY=4.55263 StartZ=0 EndX=6.84365 EndY=5.84503 EndZ=0
    g56: LineSegment StartX=8.31492 StartY=3.44415 StartZ=0 EndX=8.75133 EndY=2.10101 EndZ=0
    g57: LineSegment StartX=8.75133 StartY=2.10101 StartZ=0 EndX=6.81631 EndY=1.63645 EndZ=0
    g58: LineSegment StartX=6.81631 StartY=1.63645 StartZ=0 EndX=6.4764 EndY=2.68261 EndZ=0
    g59: LineSegment StartX=6.4764 StartY=2.68261 StartZ=0 EndX=8.31492 EndY=3.44415 EndZ=0
    g60: LineSegment StartX=8.97226 StartY=0.706132 StartZ=0 EndX=8.97226 EndY=-0.706132 EndZ=0
    g61: LineSegment StartX=8.97226 StartY=-0.706132 StartZ=0 EndX=6.98839 EndY=-0.549998 EndZ=0
    g62: LineSegment StartX=6.98839 StartY=-0.549998 StartZ=0 EndX=6.98839 EndY=0.549998 EndZ=0
    g63: LineSegment StartX=6.98839 StartY=0.549998 StartZ=0 EndX=8.97226 EndY=0.706132 EndZ=0
    g64: LineSegment StartX=8.75133 StartY=-2.10101 StartZ=0 EndX=8.31492 EndY=-3.44415 EndZ=0
    g65: LineSegment StartX=8.31492 StartY=-3.44415 StartZ=0 EndX=6.4764 EndY=-2.68261 EndZ=0
    g66: LineSegment StartX=6.4764 StartY=-2.68261 StartZ=0 EndX=6.81631 EndY=-1.63645 EndZ=0
    g67: LineSegment StartX=6.81631 StartY=-1.63645 StartZ=0 EndX=8.75133 EndY=-2.10101 EndZ=0
    g68: LineSegment StartX=7.67376 StartY=-4.70249 StartZ=0 EndX=6.84365 EndY=-5.84503 EndZ=0
    g69: LineSegment StartX=6.84365 StartY=-5.84503 StartZ=0 EndX=5.33045 EndY=-4.55263 EndZ=0
    g70: LineSegment StartX=5.33045 StartY=-4.55263 StartZ=0 EndX=5.97701 EndY=-3.66271 EndZ=0
    g71: LineSegment StartX=5.97701 StartY=-3.66271 StartZ=0 EndX=7.67376 EndY=-4.70249 EndZ=0
    g72: LineSegment StartX=5.84503 StartY=-6.84365 StartZ=0 EndX=4.70249 EndY=-7.67376 EndZ=0
    g73: LineSegment StartX=4.70249 StartY=-7.67376 StartZ=0 EndX=3.66271 EndY=-5.97701 EndZ=0
    g74: LineSegment StartX=3.66271 StartY=-5.97701 StartZ=0 EndX=4.55263 EndY=-5.33045 EndZ=0
    g75: LineSegment StartX=4.55263 StartY=-5.33045 StartZ=0 EndX=5.84503 EndY=-6.84365 EndZ=0
    g76: LineSegment StartX=3.44415 StartY=-8.31492 StartZ=0 EndX=2.10101 EndY=-8.75133 EndZ=0
    g77: LineSegment StartX=2.10101 StartY=-8.75133 StartZ=0 EndX=1.63645 EndY=-6.81631 EndZ=0
    g78: LineSegment StartX=1.63645 StartY=-6.81631 StartZ=0 EndX=2.68261 EndY=-6.4764 EndZ=0
    g79: LineSegment StartX=2.68261 StartY=-6.4764 StartZ=0 EndX=3.44415 EndY=-8.31492 EndZ=0
    g80: LineSegment StartX=0.706132 StartY=-8.97226 StartZ=0 EndX=-0.706132 EndY=-8.97226 EndZ=0
    g81: LineSegment StartX=-0.706132 StartY=-8.97226 StartZ=0 EndX=-0.549998 EndY=-6.98839 EndZ=0
    g82: LineSegment StartX=-0.549998 StartY=-6.98839 StartZ=0 EndX=0.549998 EndY=-6.98839 EndZ=0
    g83: LineSegment StartX=0.549998 StartY=-6.98839 StartZ=0 EndX=0.706132 EndY=-8.97226 EndZ=0
    g84: LineSegment StartX=-2.10101 StartY=-8.75133 StartZ=0 EndX=-3.44415 EndY=-8.31492 EndZ=0
    g85: LineSegment StartX=-3.44415 StartY=-8.31492 StartZ=0 EndX=-2.68261 EndY=-6.4764 EndZ=0
    g86: LineSegment StartX=-2.68261 StartY=-6.4764 StartZ=0 EndX=-1.63645 EndY=-6.81631 EndZ=0
    g87: LineSegment StartX=-1.63645 StartY=-6.81631 StartZ=0 EndX=-2.10101 EndY=-8.75133 EndZ=0
    g88: LineSegment StartX=-4.70249 StartY=-7.67376 StartZ=0 EndX=-5.84503 EndY=-6.84365 EndZ=0
    g89: LineSegment StartX=-5.84503 StartY=-6.84365 StartZ=0 EndX=-4.55263 EndY=-5.33045 EndZ=0
    g90: LineSegment StartX=-4.55263 StartY=-5.33045 StartZ=0 EndX=-3.66271 EndY=-5.97701 EndZ=0
    g91: LineSegment StartX=-3.66271 StartY=-5.97701 StartZ=0 EndX=-4.70249 EndY=-7.67376 EndZ=0
    g92: LineSegment StartX=-6.84365 StartY=-5.84503 StartZ=0 EndX=-7.67376 EndY=-4.70249 EndZ=0
    g93: LineSegment StartX=-7.67376 StartY=-4.70249 StartZ=0 EndX=-5.97701 EndY=-3.66271 EndZ=0
    g94: LineSegment StartX=-5.97701 StartY=-3.66271 StartZ=0 EndX=-5.33045 EndY=-4.55263 EndZ=0
    g95: LineSegment StartX=-5.33045 StartY=-4.55263 StartZ=0 EndX=-6.84365 EndY=-5.84503 EndZ=0
    g96: LineSegment StartX=-8.31492 StartY=-3.44415 StartZ=0 EndX=-6.4764 EndY=-2.68261 EndZ=0
    g97: LineSegment StartX=-6.4764 StartY=-2.68261 StartZ=0 EndX=-6.81631 EndY=-1.63645 EndZ=0
    g98: LineSegment StartX=-8.31492 StartY=-3.44415 StartZ=0 EndX=-8.75133 EndY=-2.10101 EndZ=0
    g99: LineSegment StartX=-8.75133 StartY=-2.10101 StartZ=0 EndX=-6.81631 EndY=-1.63645 EndZ=0
    g100: LineSegment StartX=-8.97226 StartY=-0.706132 StartZ=0 EndX=-8.97226 EndY=0.706132 EndZ=0
    g101: LineSegment StartX=-8.97226 StartY=0.706132 StartZ=0 EndX=-6.98839 EndY=0.549998 EndZ=0
    g102: LineSegment StartX=-6.98839 StartY=0.549998 StartZ=0 EndX=-6.98839 EndY=-0.549998 EndZ=0
    g103: LineSegment StartX=-6.98839 StartY=-0.549998 StartZ=0 EndX=-8.97226 EndY=-0.706132 EndZ=0
    g104: LineSegment StartX=-8.75133 StartY=2.10101 StartZ=0 EndX=-8.31492 EndY=3.44415 EndZ=0
    g105: LineSegment StartX=-8.31492 StartY=3.44415 StartZ=0 EndX=-6.4764 EndY=2.68261 EndZ=0
    g106: LineSegment StartX=-6.4764 StartY=2.68261 StartZ=0 EndX=-6.81631 EndY=1.63645 EndZ=0
    g107: LineSegment StartX=-6.81631 StartY=1.63645 StartZ=0 EndX=-8.75133 EndY=2.10101 EndZ=0
    g108: LineSegment StartX=-7.67376 StartY=4.70249 StartZ=0 EndX=-5.97701 EndY=3.66271 EndZ=0
    g109: LineSegment StartX=-5.97701 StartY=3.66271 StartZ=0 EndX=-5.33045 EndY=4.55263 EndZ=0
    g110: LineSegment StartX=-5.33045 StartY=4.55263 StartZ=0 EndX=-6.84365 EndY=5.84503 EndZ=0
    g111: LineSegment StartX=-6.84365 StartY=5.84503 StartZ=0 EndX=-7.67376 EndY=4.70249 EndZ=0
    g112: LineSegment StartX=-5.84503 StartY=6.84365 StartZ=0 EndX=-4.55263 EndY=5.33045 EndZ=0
    g113: LineSegment StartX=-4.55263 StartY=5.33045 StartZ=0 EndX=-3.66271 EndY=5.97701 EndZ=0
    g114: LineSegment StartX=-3.66271 StartY=5.97701 StartZ=0 EndX=-4.70249 EndY=7.67376 EndZ=0
    g115: LineSegment StartX=-4.70249 StartY=7.67376 StartZ=0 EndX=-5.84503 EndY=6.84365 EndZ=0
    g116: LineSegment StartX=-3.44415 StartY=8.31492 StartZ=0 EndX=-2.68261 EndY=6.4764 EndZ=0
    g117: LineSegment StartX=-2.68261 StartY=6.4764 StartZ=0 EndX=-1.63645 EndY=6.81631 EndZ=0
    g118: LineSegment StartX=-1.63645 StartY=6.81631 StartZ=0 EndX=-2.10101 EndY=8.75133 EndZ=0
    g119: LineSegment StartX=-2.10101 StartY=8.75133 StartZ=0 EndX=-3.44415 EndY=8.31492 EndZ=0
  constraints (320):
    c: PointOnObject(g25,g-4)
    c: PointOnObject(g24,g-4)
    c: PointOnObject(g23,g-4)
    c: PointOnObject(g22,g-4)
    c: PointOnObject(g21,g-4)
    c: PointOnObject(g38,g-4)
    c: PointOnObject(g37,g-4)
    c: Coincident(g34,g-1)
    c: Coincident(g33,g34)
    c: Coincident(g32,g33)
    c: Coincident(g31,g32)
    c: Coincident(g29,g31)
    c: Coincident(g28,g29)
    c: Coincident(g27,g28)
    c: Coincident(g37,g27)
    c: Coincident(g26,g27)
    c: Coincident(g21,g26)
    c: Coincident(g22,g21)
    c: Coincident(g23,g21)
    c: Coincident(g25,g21)
    c: Coincident(g30,g21)
    c: Coincident(g38,g21)
    c: Coincident(g24,g21)
    c: Coincident(g1,g21)
    c: Coincident(g0,g1)
    c: Coincident(g2,g0)
    c: Coincident(g4,g0)
    c: Coincident(g35,g0)
    c: Coincident(g36,g0)
    c: Coincident(g20,g0)
    c: Coincident(g19,g0)
    c: Coincident(g18,g0)
    c: Coincident(g17,g0)
    c: Coincident(g16,g0)
    c: Coincident(g15,g0)
    c: Coincident(g14,g0)
    c: Coincident(g13,g0)
    c: Coincident(g12,g0)
    c: Coincident(g11,g0)
    c: Coincident(g10,g0)
    c: Coincident(g9,g0)
    c: Coincident(g8,g0)
    c: Coincident(g7,g0)
    c: Coincident(g6,g0)
    c: Coincident(g5,g0)
    c: Coincident(g3,g0)
    c: Coincident(g39,g0)
    c: PointOnObject(g39,g-4)
    c: PointOnObject(g0,g-4)
    c: PointOnObject(g1,g-4)
    c: PointOnObject(g2,g-4)
    c: PointOnObject(g3,g-4)
    c: PointOnObject(g4,g-4)
    c: PointOnObject(g5,g-4)
    c: PointOnObject(g6,g-4)
    c: PointOnObject(g7,g-4)
    c: PointOnObject(g8,g-4)
    c: PointOnObject(g9,g-4)
    c: PointOnObject(g10,g-4)
    c: PointOnObject(g11,g-4)
    c: PointOnObject(g12,g-4)
    c: PointOnObject(g13,g-4)
    c: PointOnObject(g14,g-4)
    c: PointOnObject(g15,g-4)
    c: PointOnObject(g16,g-4)
    c: PointOnObject(g17,g-4)
    c: PointOnObject(g18,g-4)
    c: PointOnObject(g19,g-4)
    c: PointOnObject(g20,g-4)
    c: PointOnObject(g36,g-4)
    c: PointOnObject(g35,g-4)
    c: PointOnObject(g34,g-4)
    c: PointOnObject(g33,g-4)
    c: PointOnObject(g32,g-4)
    c: PointOnObject(g31,g-4)
    c: PointOnObject(g30,g-4)
    c: PointOnObject(g29,g-4)
    c: PointOnObject(g28,g-4)
    c: PointOnObject(g27,g-4)
    c: PointOnObject(g26,g-4)
    c: Angle(g-2,g39) = 0.0785398
    c: Angle(g39,g25) = 0.15708
    c: Angle(g25,g24) = 0.15708
    c: Angle(g24,g23) = 0.15708
    c: Angle(g23,g22) = 0.15708
    c: Angle(g22,g21) = 0.15708
    c: Angle(g21,g38) = 0.15708
    c: Angle(g38,g37) = 0.15708
    c: Angle(g37,g26) = 0.15708
    c: Angle(g26,g27) = 0.15708
    c: Angle(g27,g28) = 0.15708
    c: Angle(g28,g29) = 0.15708
    c: Angle(g29,g30) = 0.15708
    c: Angle(g30,g31) = 0.15708
    c: Angle(g31,g32) = 0.15708
    c: Angle(g32,g33) = 0.15708
    c: Angle(g33,g34) = 0.15708
    c: Angle(g34,g35) = 0.15708
    c: Angle(g35,g36) = 0.15708
    c: Angle(g36,g20) = 0.15708
    c: Angle(g20,g19) = 0.15708
    c: Angle(g19,g18) = 0.15708
    c: Angle(g18,g17) = 0.15708
    c: Angle(g17,g16) = 0.15708
    c: Angle(g16,g15) = 0.15708
    c: Angle(g15,g14) = 0.15708
    c: Angle(g14,g13) = 0.15708
    c: Angle(g13,g12) = 0.15708
    c: Angle(g12,g11) = 0.15708
    c: Angle(g11,g10) = 0.15708
    c: Angle(g10,g9) = 0.15708
    c: Angle(g9,g8) = 0.15708
    c: Angle(g8,g7) = 0.15708
    c: Angle(g7,g6) = 0.15708
    c: Angle(g6,g5) = 0.15708
    c: Angle(g5,g4) = 0.15708
    c: Angle(g4,g3) = 0.15708
    c: Angle(g3,g2) = 0.15708
    c: Angle(g2,g1) = 0.15708
    c: Angle(g1,g0) = 0.15708
    c: Coincident(g40,g0)
    c: Coincident(g40,g39)
    c: Coincident(g41,g39)
    c: PointOnObject(g41,g39)
    c: Coincident(g42,g41)
    c: PointOnObject(g42,g0)
    c: Horizontal(g42)
    c: Coincident(g43,g42)
    c: Coincident(g43,g0)
    c: Coincident(g44,g1)
    c: PointOnObject(g44,g1)
    c: Coincident(g45,g44)
    c: PointOnObject(g45,g2)
    c: Coincident(g46,g45)
    c: Coincident(g46,g2)
    c: Coincident(g47,g2)
    c: Coincident(g47,g1)
    c: Coincident(g48,g3)
    c: Coincident(g48,g4)
    c: Coincident(g49,g4)
    c: PointOnObject(g49,g4)
    c: Coincident(g50,g49)
    c: PointOnObject(g50,g3)
    c: Coincident(g51,g50)
    c: Coincident(g51,g48)
    c: Coincident(g52,g5)
    c: Coincident(g52,g6)
    c: Coincident(g53,g6)
    c: PointOnObject(g53,g6)
    c: Coincident(g54,g53)
    c: PointOnObject(g54,g5)
    c: Coincident(g55,g54)
    c: Coincident(g55,g5)
    c: Coincident(g56,g7)
    c: Coincident(g56,g8)
    c: Coincident(g57,g56)
    c: PointOnObject(g57,g8)
    c: Coincident(g58,g57)
    c: PointOnObject(g58,g7)
    c: Coincident(g59,g58)
    c: Coincident(g59,g7)
    c: Coincident(g60,g9)
    c: Coincident(g60,g10)
    c: Coincident(g61,g60)
    c: PointOnObject(g61,g10)
    c: Coincident(g62,g61)
    c: PointOnObject(g62,g9)
    c: Coincident(g63,g62)
    c: Coincident(g63,g9)
    c: Coincident(g64,g11)
    c: Coincident(g64,g12)
    c: Coincident(g65,g12)
    c: PointOnObject(g65,g12)
    c: Coincident(g66,g65)
    c: PointOnObject(g66,g11)
    c: Coincident(g67,g66)
    c: Coincident(g67,g11)
    c: Coincident(g68,g13)
    c: Coincident(g68,g14)
    c: Coincident(g69,g14)
    c: PointOnObject(g69,g14)
    c: Coincident(g70,g69)
    c: PointOnObject(g70,g13)
    c: Coincident(g71,g70)
    c: Coincident(g71,g13)
    c: Coincident(g72,g15)
    c: Coincident(g72,g16)
    c: Coincident(g73,g16)
    c: PointOnObject(g73,g16)
    c: Coincident(g74,g73)
    c: PointOnObject(g74,g15)
    c: Coincident(g75,g74)
    c: Coincident(g75,g72)
    c: Coincident(g76,g17)
    c: Coincident(g76,g18)
    c: Coincident(g77,g18)
    c: PointOnObject(g77,g18)
    c: Coincident(g78,g77)
    c: PointOnObject(g78,g17)
    c: Coincident(g79,g78)
    c: Coincident(g79,g17)
    c: Coincident(g80,g19)
    c: Coincident(g80,g20)
    c: Coincident(g81,g20)
    c: PointOnObject(g81,g20)
    c: Coincident(g82,g81)
    c: PointOnObject(g82,g19)
    c: Horizontal(g82)
    c: Coincident(g83,g82)
    c: Coincident(g83,g19)
    c: Coincident(g84,g36)
    c: Coincident(g84,g35)
    c: Coincident(g85,g35)
    c: PointOnObject(g85,g35)
    c: Coincident(g86,g85)
    c: PointOnObject(g86,g36)
    c: Coincident(g87,g86)
    c: Coincident(g87,g36)
    c: Coincident(g88,g34)
    c: Coincident(g88,g33)
    c: Coincident(g89,g88)
    c: PointOnObject(g89,g33)
    c: Coincident(g90,g89)
    c: PointOnObject(g90,g34)
    c: Coincident(g91,g90)
    c: Coincident(g91,g34)
    c: Coincident(g92,g32)
    c: Coincident(g92,g31)
    c: Coincident(g93,g31)
    c: PointOnObject(g93,g31)
    c: Coincident(g94,g93)
    c: PointOnObject(g94,g32)
    c: Coincident(g95,g94)
    c: Coincident(g95,g32)
    c: Coincident(g96,g30)
    c: PointOnObject(g96,g30)
    c: Coincident(g97,g96)
    c: PointOnObject(g97,g29)
    c: Coincident(g98,g30)
    c: Coincident(g98,g29)
    c: Coincident(g99,g29)
    c: Coincident(g99,g97)
    c: Coincident(g100,g28)
    c: Coincident(g100,g27)
    c: Coincident(g101,g27)
    c: PointOnObject(g101,g27)
    c: Coincident(g102,g101)
    c: PointOnObject(g102,g28)
    c: Coincident(g103,g102)
    c: Coincident(g103,g100)
    c: Coincident(g104,g26)
    c: Coincident(g104,g37)
    c: Coincident(g105,g37)
    c: PointOnObject(g105,g37)
    c: Coincident(g106,g105)
    c: PointOnObject(g106,g26)
    c: Coincident(g107,g106)
    c: Coincident(g107,g104)
    c: Coincident(g108,g38)
    c: PointOnObject(g108,g38)
    c: Coincident(g109,g108)
    c: PointOnObject(g109,g21)
    c: Coincident(g110,g109)
    c: Coincident(g110,g21)
    c: Coincident(g111,g21)
    c: Coincident(g111,g38)
    c: Coincident(g112,g22)
    c: PointOnObject(g112,g22)
    c: Coincident(g113,g112)
    c: PointOnObject(g113,g23)
    c: Coincident(g114,g113)
    c: Coincident(g114,g23)
    c: Coincident(g115,g23)
    c: Coincident(g115,g22)
    c: Coincident(g116,g24)
    c: PointOnObject(g116,g24)
    c: Coincident(g117,g116)
    c: PointOnObject(g117,g25)
    c: Coincident(g118,g117)
    c: Coincident(g118,g25)
    c: Coincident(g119,g25)
    c: Coincident(g119,g24)
    c: PointOnObject(g117,g-3)
    c: PointOnObject(g116,g-3)
    c: PointOnObject(g41,g-3)
    c: PointOnObject(g44,g-3)
    c: PointOnObject(g45,g-3)
    c: PointOnObject(g50,g-3)
    c: PointOnObject(g49,g-3)
    c: PointOnObject(g54,g-3)
    c: PointOnObject(g53,g-3)
    c: PointOnObject(g58,g-3)
    c: PointOnObject(g57,g-3)
    c: PointOnObject(g62,g-3)
    c: PointOnObject(g61,g-3)
    c: PointOnObject(g113,g-3)
    c: PointOnObject(g112,g-3)
    c: PointOnObject(g109,g-3)
    c: PointOnObject(g108,g-3)
    c: PointOnObject(g105,g-3)
    c: PointOnObject(g106,g-3)
    c: PointOnObject(g101,g-3)
    c: PointOnObject(g102,g-3)
    c: PointOnObject(g97,g-3)
    c: PointOnObject(g96,g-3)
    c: PointOnObject(g93,g-3)
    c: PointOnObject(g94,g-3)
    c: PointOnObject(g89,g-3)
    c: PointOnObject(g90,g-3)
    c: PointOnObject(g85,g-3)
    c: PointOnObject(g86,g-3)
    c: PointOnObject(g81,g-3)
    c: PointOnObject(g77,g-3)
    c: PointOnObject(g78,g-3)
    c: PointOnObject(g73,g-3)
    c: PointOnObject(g74,g-3)
    c: PointOnObject(g69,g-3)
    c: PointOnObject(g70,g-3)
    c: PointOnObject(g65,g-3)
    c: PointOnObject(g66,g-3)
FEATURE [PartDesign::Pad] Pad150
  BaseFeature = -> Pocket101
  Direction = (0,1,2e-16)
  Length = 2
  Length2 = 10
  Placement = pos=(0,0,0) rot=(1,0,0;1.5708rad)
  Profile = -> Sketch247
  ReferenceAxis = -> Sketch247 [N_Axis]
  Refine = true
  Reversed = true
  Suppressed = false
  Type = 0
FEATURE [Sketcher::SketchObject] Sketch248
  ArcFitTolerance = 1e-06
  AttachmentSupport = -> [Pad150]
  ExternalGeometry = -> [Pad150]
  FullyConstrained = true
  MakeInternals = false
  MapMode = 5
  Placement = pos=(0,0,-1e-16) rot=(0.999229,0,-0.03926;3.14159rad)
  sketch-geometry (3):
    g0: LineSegment StartX=7.01 StartY=0 StartZ=0 EndX=9 EndY=6.9e-15 EndZ=0
    g1: LineSegment StartX=9 StartY=6.9e-15 StartZ=0 EndX=9 EndY=0.5 EndZ=0
    g2: LineSegment StartX=9 StartY=0.5 StartZ=0 EndX=7.01 EndY=0 EndZ=0
  constraints (7):
    c: Coincident(g0,g-4)
    c: Coincident(g0,g-4)
    c: Coincident(g1,g0)
    c: PointOnObject(g1,g-3)
    c: Coincident(g2,g1)
    c: Coincident(g2,g0)
    c: DistanceY(g1,g1) = 0.5
FEATURE [PartDesign::SubtractivePipe] SubtractivePipe002
  AuxilleryCurvelinear = true
  AuxillerySpineTangent = false
  BaseFeature = -> Pad150
  Binormal = (0,0,0)
  Mode = 0
  Placement = pos=(0,0,0) rot=(1,0,0;1.5708rad)
  Profile = -> Sketch248
  Refine = true
  Spine = -> Pad150 [Edge2]
  SpineTangent = false
  Suppressed = false
  Transformation = 0
  Transition = 0
FEATURE [Sketcher::SketchObject] Sketch249
  ArcFitTolerance = 1e-06
  AttachmentSupport = -> [SubtractivePipe002]
  FullyConstrained = true
  MakeInternals = false
  MapMode = 5
  Placement = pos=(0,-3.5,0) rot=(1,0,0;1.5708rad)
  sketch-geometry (1):
    g0: Circle CenterX=0 CenterY=0 CenterZ=0 NormalX=0 NormalY=0 NormalZ=1 AngleXU=0 Radius=1
  constraints (2):
    c: Coincident(g0,g-1)
    c: Diameter(g0) = 2
FEATURE [PartDesign::Pocket] Pocket102
  BaseFeature = -> SubtractivePipe002
  Direction = (0,1,-2e-16)
  Length = 5
  Length2 = 5
  Placement = pos=(0,0,0) rot=(1,0,0;1.5708rad)
  Profile = -> Sketch249
  ReferenceAxis = -> Sketch249 [N_Axis]
  Refine = true
  Suppressed = false
  Type = 0
FEATURE [PartDesign::Body] Body007  label="Tire1"
  AllowCompound = false
  Group = -> [Sketch235,Pad145,Sketch236,Pocket097,Sketch237,Pocket098,Sketch238,Pocket099,Sketch239,Pad146,Sketch240,Pad147,Sketch241,Pad148,Sketch242,SubtractivePipe,Chamfer001,Sketch243,Pad149,Sketch244,SubtractivePipe001,Sketch245,Pocket100,Sketch246,Pocket101,Sketch247,Pad150,Sketch248,SubtractivePipe002,Sketch249,Pocket102]
  Origin = -> Origin007
  Placement = pos=(-49.9,-13,-1.1) rot=(0,0,1;0rad)
  Tip = -> Pocket102
COMPONENT P16 — same part as P15; its construction recipe is shown at P15.
COMPONENT P17 — recipe-attached ("Right_Inner_Arm001", modeled in this document).
Construction recipe (the document's own serialized feature program — sketch geometry with constraints, then the solid features built on it; lengths are millimeters unless a unit is written):

FEATURE [Sketcher::SketchObject] Sketch261
  ArcFitTolerance = 1e-06
  AttachmentOffset = pos=(0,0,22) rot=(0,0,1;0rad)
  AttachmentSupport = -> [XZ_Plane009]
  FullyConstrained = true
  MakeInternals = false
  MapMode = 5
  Placement = pos=(0,-22,4.9e-15) rot=(1,0,0;1.5708rad)
  sketch-geometry (1):
    g0: Circle CenterX=0 CenterY=0 CenterZ=0 NormalX=0 NormalY=0 NormalZ=1 AngleXU=0 Radius=7.25
  constraints (2):
    c: Coincident(g0,g-1)
    c: Diameter(g0) = 14.5
FEATURE [PartDesign::Pad] Pad160
  Direction = (0,-1,2e-16)
  Length = 1.5
  Length2 = 10
  Placement = pos=(0,0,0) rot=(1,0,0;1.5708rad)
  Profile = -> Sketch261
  ReferenceAxis = -> Sketch261 [N_Axis]
  Refine = true
  Suppressed = false
  Type = 0
FEATURE [Sketcher::SketchObject] Sketch262
  ArcFitTolerance = 1e-06
  AttachmentSupport = -> [Pad160]
  ExternalGeometry = -> [Pad160]
  FullyConstrained = true
  MakeInternals = false
  MapMode = 5
  Placement = pos=(0,-23.5,0) rot=(1,0,0;1.5708rad)
  sketch-geometry (15):
    g0: LineSegment StartX=-7.25 StartY=9e-16 StartZ=0 EndX=-8.95 EndY=9e-16 EndZ=0
    g1: LineSegment StartX=-8.95 StartY=9e-16 StartZ=0 EndX=-8.95 EndY=11.6 EndZ=0
    g2: LineSegment StartX=-8.95 StartY=11.6 StartZ=0 EndX=18.65 EndY=11.6 EndZ=0
    g3: ArcOfCircle CenterX=18.65 CenterY=11.1 CenterZ=0 NormalX=0 NormalY=0 NormalZ=1 AngleXU=0 Radius=0.5 StartAngle=1.4e-15 EndAngle=1.5708
    g4: LineSegment StartX=19.15 StartY=11.1 StartZ=0 EndX=19.15 EndY=9.225 EndZ=0
    g5: ArcOfCircle CenterX=18.65 CenterY=9.225 CenterZ=0 NormalX=0 NormalY=0 NormalZ=1 AngleXU=0 Radius=0.5 StartAngle=4.71239 EndAngle=6.28319
    g6: LineSegment StartX=18.65 StartY=8.725 StartZ=0 EndX=13.85 EndY=8.725 EndZ=0
    g7: LineSegment StartX=13.85 StartY=8.725 StartZ=0 EndX=13.85 EndY=6.475 EndZ=0
    g8: LineSegment StartX=13.85 StartY=6.475 StartZ=0 EndX=18.65 EndY=6.475 EndZ=0
    g9: ArcOfCircle CenterX=18.65 CenterY=5.975 CenterZ=0 NormalX=0 NormalY=0 NormalZ=1 AngleXU=0 Radius=0.5 StartAngle=7e-16 EndAngle=1.5708
    g10: LineSegment StartX=19.15 StartY=5.975 StartZ=0 EndX=19.15 EndY=4.1 EndZ=0
    g11: ArcOfCircle CenterX=18.65 CenterY=4.1 CenterZ=0 NormalX=0 NormalY=0 NormalZ=1 AngleXU=0 Radius=0.5 StartAngle=4.71239 EndAngle=6.28319
    g12: LineSegment StartX=18.65 StartY=3.6 StartZ=0 EndX=7.25 EndY=3.6 EndZ=0
    g13: LineSegment StartX=7.25 StartY=3.6 StartZ=0 EndX=7.25 EndY=0 EndZ=0
    g14: ArcOfCircle CenterX=0 CenterY=0 CenterZ=0 NormalX=0 NormalY=0 NormalZ=1 AngleXU=0 Radius=7.25 StartAngle=0 EndAngle=3.14159
  constraints (50):
    c: PointOnObject(g0,g-3)
    c: PointOnObject(g0,g-1)
    c: Horizontal(g0)
    c: Coincident(g1,g0)
    c: Vertical(g1)
    c: Coincident(g2,g1)
    c: Horizontal(g2)
    c: Coincident(g3,g2)
    c: Coincident(g4,g3)
    c: Coincident(g5,g4)
    c: Coincident(g6,g5)
    c: Horizontal(g6)
    c: Coincident(g7,g6)
    c: Vertical(g7)
    c: Coincident(g8,g7)
    c: Horizontal(g8)
    c: Coincident(g9,g8)
    c: Coincident(g10,g9)
    c: Coincident(g11,g10)
    c: Coincident(g12,g11)
    c: Coincident(g13,g12)
    c: DistanceX(g0,g0) = 1.7
    c: DistanceY(g1,g1) = 11.6
    c: DistanceY(g7,g7) = 2.25
    c: Vertical(g4)
    c: Vertical(g10)
    c: Horizontal(g12)
    c: Vertical(g13)
    c: DistanceX(g8,g9) = 0
    c: DistanceY(g9,g9) = 0
    c: DistanceX(g11,g11) = 0
    c: DistanceY(g11,g10) = 0
    c: DistanceY(g11,g8) = 2.875
    c: Radius(g9) = 0.5
    c: Radius(g11) = 0.5
    c: DistanceY(g5,g4) = 0
    c: DistanceX(g5,g5) = 0
    c: DistanceX(g2,g3) = 0
    c: DistanceY(g3,g3) = 0
    c: DistanceX(g12,g10) = 11.9
    c: DistanceX(g12,g4) = 11.9
    c: Radius(g3) = 0.5
    c: Radius(g5) = 0.5
    c: DistanceX(g6,g4) = 5.3
    c: Coincident(g14,g0)
    c: Coincident(g14,g13)
    c: Coincident(g14,g-1)
    c: DistanceY(g14,g13) = 0
    c: DistanceY(g5,g2) = 2.875
    c: DistanceY(g11,g2) = 8
FEATURE [PartDesign::Pad] Pad161
  BaseFeature = -> Pad160
  Direction = (0,-1,2e-16)
  Length = 1.5
  Length2 = 10
  Placement = pos=(0,0,0) rot=(1,0,0;1.5708rad)
  Profile = -> Sketch262
  ReferenceAxis = -> Sketch262 [N_Axis]
  Refine = true
  Reversed = true
  Suppressed = false
  Type = 0
FEATURE [Sketcher::SketchObject] Sketch263
  ArcFitTolerance = 1e-06
  AttachmentSupport = -> [Pad161]
  ExternalGeometry = -> [Pad161]
  FullyConstrained = true
  MakeInternals = false
  MapMode = 5
  Placement = pos=(0,1.6e-15,3.6) rot=(1,0,0;3.14159rad)
  sketch-geometry (3):
    g0: ArcOfCircle CenterX=16.5137 CenterY=24.9317 CenterZ=0 NormalX=0 NormalY=0 NormalZ=1 AngleXU=0 Radius=3 StartAngle=4.92611 EndAngle=5.78567
    g1: LineSegment StartX=19.15 StartY=23.5 StartZ=0 EndX=19.15 EndY=22 EndZ=0
    g2: LineSegment StartX=19.15 StartY=22 StartZ=0 EndX=17.15 EndY=22 EndZ=0
  constraints (8):
    c: Coincident(g0,g-3)
    c: PointOnObject(g0,g-4)
    c: Coincident(g1,g0)
    c: Coincident(g1,g-3)
    c: Coincident(g2,g1)
    c: Coincident(g2,g0)
    c: DistanceX(g2,g2) = 2
    c: Radius(g0) = 3
FEATURE [PartDesign::Pocket] Pocket105
  BaseFeature = -> Pad161
  Direction = (0,0,1)
  Length = 8
  Length2 = 5
  Placement = pos=(0,0,0) rot=(1,0,0;1.5708rad)
  Profile = -> Sketch263
  ReferenceAxis = -> Sketch263 [N_Axis]
  Refine = true
  Suppressed = false
  Type = 0
FEATURE [Sketcher::SketchObject] Sketch264
  ArcFitTolerance = 1e-06
  AttachmentSupport = -> [Pocket105]
  FullyConstrained = true
  MakeInternals = false
  MapMode = 5
  Placement = pos=(0,-23.5,9.2e-15) rot=(1,0,0;1.5708rad)
  sketch-geometry (1):
    g0: Circle CenterX=0 CenterY=0 CenterZ=0 NormalX=0 NormalY=0 NormalZ=1 AngleXU=0 Radius=0.75
  constraints (2):
    c: Coincident(g0,g-1)
    c: Diameter(g0) = 1.5
FEATURE [PartDesign::Pocket] Pocket106
  BaseFeature = -> Pocket105
  Direction = (0,1,-2e-16)
  Length = 5
  Length2 = 5
  Placement = pos=(0,0,0) rot=(1,0,0;1.5708rad)
  Profile = -> Sketch264
  ReferenceAxis = -> Sketch264 [N_Axis]
  Refine = true
  Suppressed = false
  Type = 0
FEATURE [Sketcher::SketchObject] Sketch265
  ArcFitTolerance = 1e-06
  AttachmentSupport = -> [Pocket106]
  ExternalGeometry = -> [Pocket106]
  FullyConstrained = true
  MakeInternals = false
  MapMode = 5
  Placement = pos=(0,-22,8.6e-15) rot=(-1,0,0;1.5708rad)
  sketch-geometry (5):
    g0: LineSegment StartX=-8.95 StartY=-11.6 StartZ=0 EndX=11.05 EndY=-11.6 EndZ=0
    g1: LineSegment StartX=-8.95 StartY=-11.6 StartZ=0 EndX=-8.95 EndY=-5.6 EndZ=0
    g2: LineSegment StartX=-8.95 StartY=-5.6 StartZ=0 EndX=9.05 EndY=-5.6 EndZ=0
    g3: ArcOfCircle CenterX=9.05 CenterY=-7.6 CenterZ=0 NormalX=0 NormalY=0 NormalZ=1 AngleXU=0 Radius=2 StartAngle=1e-16 EndAngle=1.5708
    g4: LineSegment StartX=11.05 StartY=-7.6 StartZ=0 EndX=11.05 EndY=-11.6 EndZ=0
  constraints (16):
    c: Coincident(g0,g-4)
    c: PointOnObject(g0,g-4)
    c: Coincident(g1,g0)
    c: Coincident(g2,g1)
    c: Horizontal(g2)
    c: Coincident(g3,g2)
    c: Coincident(g4,g3)
    c: Coincident(g4,g0)
    c: DistanceY(g1,g1) = 6
    c: Vertical(g4)
    c: DistanceX(g2,g3) = 0
    c: DistanceY(g3,g3) = 0
    c: DistanceX(g0,g0) = 20
    c: Radius(g3) = 2
    c: PointOnObject(g1,g-3)
    c: DistanceY(g-4,g-5) = 8
FEATURE [PartDesign::Pad] Pad162
  BaseFeature = -> Pocket106
  Direction = (0,1,2e-16)
  Length = 0.5
  Length2 = 10
  Placement = pos=(0,0,0) rot=(1,0,0;1.5708rad)
  Profile = -> Sketch265
  ReferenceAxis = -> Sketch265 [N_Axis]
  Refine = true
  Suppressed = false
  Type = 0
FEATURE [Sketcher::SketchObject] Sketch266
  ArcFitTolerance = 1e-06
  AttachmentSupport = -> [Pad162]
  ExternalGeometry = -> [Pad162]
  FullyConstrained = true
  MakeInternals = false
  MapMode = 5
  Placement = pos=(0,-21.5,-1.29e-14) rot=(-1,0,0;1.5708rad)
  sketch-geometry (1):
    g0: Circle CenterX=-3.9 CenterY=-9.1 CenterZ=0 NormalX=0 NormalY=0 NormalZ=1 AngleXU=0 Radius=2.55
  constraints (3):
    c: Diameter(g0) = 5.1
    c: DistanceX(g-4,g0) = 5.05
    c: DistanceY(g-4,g0) = 2.5
FEATURE [PartDesign::Pad] Pad163
  BaseFeature = -> Pad162
  Direction = (0,1,2e-16)
  Length = 9
  Length2 = 10
  Placement = pos=(0,0,0) rot=(1,0,0;1.5708rad)
  Profile = -> Sketch266
  ReferenceAxis = -> Sketch266 [N_Axis]
  Refine = true
  Suppressed = false
  Type = 0
FEATURE [Sketcher::SketchObject] Sketch269
  ArcFitTolerance = 1e-06
  AttachmentSupport = -> [Pad163]
  FullyConstrained = true
  MakeInternals = false
  MapMode = 5
  Placement = pos=(0,-23.5,9.2e-15) rot=(1,0,0;1.5708rad)
  sketch-geometry (1):
    g0: Circle CenterX=0 CenterY=0 CenterZ=0 NormalX=0 NormalY=0 NormalZ=1 AngleXU=0 Radius=2.45
  constraints (2):
    c: Coincident(g0,g-1)
    c: Diameter(g0) = 4.9
FEATURE [PartDesign::Pad] Pad164
  BaseFeature = -> Pad163
  Direction = (0,-1,2e-16)
  Length = 2
  Length2 = 10
  Placement = pos=(0,0,0) rot=(1,0,0;1.5708rad)
  Profile = -> Sketch269
  ReferenceAxis = -> Sketch269 [N_Axis]
  Refine = true
  Suppressed = false
  Type = 0
FEATURE [Sketcher::SketchObject] Sketch270
  ArcFitTolerance = 1e-06
  AttachmentSupport = -> [Pad164]
  FullyConstrained = true
  MakeInternals = false
  MapMode = 5
  Placement = pos=(0,-25.5,0) rot=(1,0,0;1.5708rad)
  sketch-geometry (1):
    g0: Circle CenterX=0 CenterY=0 CenterZ=0 NormalX=0 NormalY=0 NormalZ=1 AngleXU=0 Radius=0.75
  constraints (2):
    c: Coincident(g0,g-1)
    c: Radius(g0) = 0.75
FEATURE [PartDesign::Pocket] Pocket109
  BaseFeature = -> Pad164
  Direction = (0,1,-2e-16)
  Length = 5
  Length2 = 5
  Placement = pos=(0,0,0) rot=(1,0,0;1.5708rad)
  Profile = -> Sketch270
  ReferenceAxis = -> Sketch270 [N_Axis]
  Refine = true
  Suppressed = false
  Type = 0
FEATURE [PartDesign::Pad] Pad165
  BaseFeature = -> Pocket109
  Direction = (0,1,2e-16)
  Length = 2
  Length2 = 10
  Placement = pos=(0,0,0) rot=(1,0,0;1.5708rad)
  Profile = -> Sketch266
  ReferenceAxis = -> Sketch266 [N_Axis]
  Refine = true
  Reversed = true
  Suppressed = false
  Type = 0
FEATURE [Sketcher::SketchObject] Sketch271
  ArcFitTolerance = 1e-06
  AttachmentSupport = -> [Pad165]
  ExternalGeometry = -> [Pad165]
  FullyConstrained = true
  MakeInternals = false
  MapMode = 5
  Placement = pos=(0,-21.5,-1.29e-14) rot=(-1,0,0;1.5708rad)
  sketch-geometry (1):
    g0: Circle CenterX=9.05 CenterY=-7.6 CenterZ=0 NormalX=0 NormalY=0 NormalZ=1 AngleXU=0 Radius=1
  constraints (2):
    c: Coincident(g0,g-3)
    c: Diameter(g0) = 2
FEATURE [PartDesign::Pocket] Pocket110
  BaseFeature = -> Pad165
  Direction = (0,-1,-2e-16)
  Length = 5
  Length2 = 5
  Placement = pos=(0,0,0) rot=(1,0,0;1.5708rad)
  Profile = -> Sketch271
  ReferenceAxis = -> Sketch271 [N_Axis]
  Refine = true
  Suppressed = false
  Type = 0
FEATURE [Sketcher::SketchObject] Sketch272
  ArcFitTolerance = 1e-06
  AttachmentSupport = -> [Pocket110]
  ExternalGeometry = -> [Pocket110]
  FullyConstrained = true
  MakeInternals = false
  MapMode = 5
  Placement = pos=(0,-21.5,-1.29e-14) rot=(-1,0,0;1.5708rad)
  sketch-geometry (1):
    g0: Circle CenterX=9.05 CenterY=-7.6 CenterZ=0 NormalX=0 NormalY=0 NormalZ=1 AngleXU=0 Radius=2
  constraints (2):
    c: Coincident(g0,g-3)
    c: Radius(g0) = 2
FEATURE [PartDesign::Pocket] Pocket111
  BaseFeature = -> Pocket110
  Direction = (0,-1,-2e-16)
  Length = 1
  Length2 = 5
  Placement = pos=(0,0,0) rot=(1,0,0;1.5708rad)
  Profile = -> Sketch272
  ReferenceAxis = -> Sketch272 [N_Axis]
  Refine = true
  Suppressed = false
  Type = 0
FEATURE [Sketcher::SketchObject] Sketch273
  ArcFitTolerance = 1e-06
  AttachmentSupport = -> [Pocket111]
  ExternalGeometry = -> [Pocket111]
  FullyConstrained = true
  MakeInternals = false
  MapMode = 5
  Placement = pos=(-5.7e-15,-12.5,-1e-14) rot=(-1,0,0;1.5708rad)
  sketch-geometry (1):
    g0: Circle CenterX=-3.9 CenterY=-9.1 CenterZ=0 NormalX=0 NormalY=0 NormalZ=1 AngleXU=0 Radius=0.75
  constraints (2):
    c: Coincident(g0,g-3)
    c: Diameter(g0) = 1.5
FEATURE [PartDesign::Pocket] Pocket112
  BaseFeature = -> Pocket111
  Direction = (0,-1,-2e-16)
  Length = 1.5
  Length2 = 5
  Placement = pos=(0,0,0) rot=(1,0,0;1.5708rad)
  Profile = -> Sketch273
  ReferenceAxis = -> Sketch273 [N_Axis]
  Refine = true
  Suppressed = false
  Type = 0
FEATURE [Sketcher::SketchObject] Sketch274
  ArcFitTolerance = 1e-06
  AttachmentSupport = -> [Pocket112]
  ExternalGeometry = -> [Pocket112]
  FullyConstrained = true
  MakeInternals = false
  MapMode = 5
  Placement = pos=(0,-23.5,1.5e-14) rot=(1,0,0;1.5708rad)
  sketch-geometry (1):
    g0: Circle CenterX=-3.9 CenterY=9.1 CenterZ=0 NormalX=0 NormalY=0 NormalZ=1 AngleXU=0 Radius=1.5
  constraints (2):
    c: Coincident(g0,g-3)
    c: Diameter(g0) = 3
FEATURE [PartDesign::Pocket] Pocket113
  BaseFeature = -> Pocket112
  Direction = (0,1,-2e-16)
  Length = 9.5
  Length2 = 5
  Placement = pos=(0,0,0) rot=(1,0,0;1.5708rad)
  Profile = -> Sketch274
  ReferenceAxis = -> Sketch274 [N_Axis]
  Refine = true
  Suppressed = false
  Type = 0
FEATURE [Sketcher::SketchObject] Sketch275
  ArcFitTolerance = 1e-06
  AttachmentSupport = -> [Pocket113]
  ExternalGeometry = -> [Pocket113]
  FullyConstrained = true
  MakeInternals = false
  MapMode = 5
  Placement = pos=(0,-23.5,1.5e-14) rot=(1,0,0;1.5708rad)
  sketch-geometry (2):
    g0: Circle CenterX=9.05 CenterY=7.6 CenterZ=0 NormalX=0 NormalY=0 NormalZ=1 AngleXU=0 Radius=2.45
    g1: Circle CenterX=9.05 CenterY=7.6 CenterZ=0 NormalX=0 NormalY=0 NormalZ=1 AngleXU=0 Radius=1.00001
  constraints (4):
    c: Coincident(g0,g-3)
    c: Coincident(g1,g0)
    c: Tangent(g1,g-3)
    c: Diameter(g0) = 4.9
FEATURE [PartDesign::Pad] Pad166
  BaseFeature = -> Pocket113
  Direction = (0,-1,2e-16)
  Length = 1
  Length2 = 10
  Placement = pos=(0,0,0) rot=(1,0,0;1.5708rad)
  Profile = -> Sketch275
  ReferenceAxis = -> Sketch275 [N_Axis]
  Refine = true
  Suppressed = false
  Type = 0
FEATURE [Sketcher::SketchObject] Sketch276
  ArcFitTolerance = 1e-06
  AttachmentSupport = -> [Pad166]
  ExternalGeometry = -> [Pad166]
  FullyConstrained = true
  MakeInternals = false
  MapMode = 5
  Placement = pos=(0,-23.5,1.5e-14) rot=(1,0,0;1.5708rad)
  sketch-geometry (8):
    g0: LineSegment StartX=14.05 StartY=6.475 StartZ=0 EndX=14.05 EndY=5.075 EndZ=0
    g1: LineSegment StartX=14.05 StartY=5.075 StartZ=0 EndX=16.85 EndY=5.075 EndZ=0
    g2: LineSegment StartX=16.85 StartY=5.075 StartZ=0 EndX=16.85 EndY=6.475 EndZ=0
    g3: LineSegment StartX=16.85 StartY=6.475 StartZ=0 EndX=14.05 EndY=6.475 EndZ=0
    g4: LineSegment StartX=14.05 StartY=10.125 StartZ=0 EndX=14.05 EndY=8.725 EndZ=0
    g5: LineSegment StartX=14.05 StartY=8.725 StartZ=0 EndX=16.85 EndY=8.725 EndZ=0
    g6: LineSegment StartX=16.85 StartY=8.725 StartZ=0 EndX=16.85 EndY=10.125 EndZ=0
    g7: LineSegment StartX=16.85 StartY=10.125 StartZ=0 EndX=14.05 EndY=10.125 EndZ=0
  constraints (24):
    c: Coincident(g0,g1)
    c: Coincident(g1,g2)
    c: Coincident(g2,g3)
    c: Coincident(g3,g0)
    c: Vertical(g0)
    c: Vertical(g2)
    c: Horizontal(g1)
    c: Horizontal(g3)
    c: Coincident(g4,g5)
    c: Coincident(g5,g6)
    c: Coincident(g6,g7)
    c: Coincident(g7,g4)
    c: Vertical(g4)
    c: Vertical(g6)
    c: Horizontal(g5)
    c: Horizontal(g7)
    c: DistanceY(g6,g6) = 1.4
    c: DistanceY(g2,g2) = 1.4
    c: DistanceX(g1,g1) = 2.8
    c: DistanceX(g7,g7) = 2.8
    c: DistanceX(g6,g-6) = 2.3
    c: DistanceX(g2,g-5) = 2.3
    c: PointOnObject(g5,g-7)
    c: PointOnObject(g2,g-8)
FEATURE [PartDesign::Pad] Pad167
  BaseFeature = -> Pad166
  Direction = (0,-1,2e-16)
  Length = 1
  Length2 = 10
  Placement = pos=(0,0,0) rot=(1,0,0;1.5708rad)
  Profile = -> Sketch276
  ReferenceAxis = -> Sketch276 [N_Axis]
  Refine = true
  Suppressed = false
  Type = 0
FEATURE [Sketcher::SketchObject] Sketch409
  ArcFitTolerance = 1e-06
  AttachmentSupport = -> [Pad167]
  ExternalGeometry = -> [Pad167]
  FullyConstrained = true
  MakeInternals = false
  MapMode = 5
  Placement = pos=(0,-25.5,0) rot=(1,0,0;1.5708rad)
  sketch-geometry (2):
    g0: Circle CenterX=0 CenterY=0 CenterZ=0 NormalX=0 NormalY=0 NormalZ=1 AngleXU=0 Radius=0.8
    g1: Circle CenterX=-3.9 CenterY=9.1 CenterZ=0 NormalX=0 NormalY=0 NormalZ=1 AngleXU=0 Radius=0.8
  constraints (4):
    c: Coincident(g0,g-1)
    c: Radius(g0) = 0.8
    c: Coincident(g1,g-4)
    c: Radius(g1) = 0.8
FEATURE [PartDesign::Pocket] Pocket184
  BaseFeature = -> Pad167
  Direction = (0,1,-2e-16)
  Length = 5
  Length2 = 5
  Placement = pos=(0,0,0) rot=(1,0,0;1.5708rad)
  Profile = -> Sketch409
  ReferenceAxis = -> Sketch409 [N_Axis]
  Refine = true
  Suppressed = false
  Type = 1
FEATURE [PartDesign::Body] Body009  label="Right_Inner_Arm"
  AllowCompound = false
  Group = -> [Sketch261,Pad160,Sketch262,Pad161,Sketch263,Pocket105,Sketch264,Pocket106,Sketch265,Pad162,Sketch266,Pad163,Sketch269,Pad164,Sketch270,Pocket109,Pad165,Sketch271,Pocket110,Sketch272,Pocket111,Sketch273,Pocket112,Sketch274,Pocket113,Sketch275,Pad166,Sketch276,Pad167,Sketch409,Pocket184]
  Origin = -> Origin009
  Placement = pos=(-11.6,8.4,-1.5) rot=(0,0,1;0rad)
  Tip = -> Pocket184
COMPONENT P18 — recipe-attached ("Rigt_Outer_Arm001", modeled in this document).
Construction recipe (the document's own serialized feature program — sketch geometry with constraints, then the solid features built on it; lengths are millimeters unless a unit is written):

FEATURE [PartDesign::SubShapeBinder] Binder003
  BindCopyOnChange = 0
  BindMode = 2
  ClaimChildren = false
  Context = -> Body010 [Binder003.]
  Fuse = false
  MakeFace = true
  OffsetFill = false
  OffsetIntersection = false
  OffsetJoinType = 0
  OffsetOpenResult = false
  PartialLoad = false
  Refine = true
  Relative = true
  _Version = 2
FEATURE [Sketcher::SketchObject] Sketch287
  ArcFitTolerance = 1e-06
  AttachmentSupport = -> [Binder003]
  ExternalGeometry = -> [Binder003]
  FullyConstrained = true
  MakeInternals = false
  MapMode = 5
  Placement = pos=(0,-15.1,9.5e-15) rot=(1,0,0;1.5708rad)
  sketch-geometry (18):
    g0: LineSegment StartX=5.25 StartY=3.45 StartZ=0 EndX=5.25 EndY=4.85 EndZ=0
    g1: LineSegment StartX=5.25 StartY=4.85 StartZ=0 EndX=7.05 EndY=4.85 EndZ=0
    g2: LineSegment StartX=5.25 StartY=8.75 StartZ=0 EndX=5.25 EndY=7.35 EndZ=0
    g3: LineSegment StartX=5.25 StartY=7.35 StartZ=0 EndX=7.05 EndY=7.35 EndZ=0
    g4: ArcOfCircle CenterX=7.05 CenterY=7.85 CenterZ=0 NormalX=0 NormalY=0 NormalZ=1 AngleXU=0 Radius=0.500004 StartAngle=4.7124 EndAngle=6.28318
    g5: ArcOfCircle CenterX=7.05 CenterY=4.35 CenterZ=0 NormalX=0 NormalY=0 NormalZ=1 AngleXU=0 Radius=0.500004 StartAngle=7.39517e-06 EndAngle=1.57079
    g6: ArcOfCircle CenterX=7.05 CenterY=2.6 CenterZ=0 NormalX=0 NormalY=0 NormalZ=1 AngleXU=0 Radius=0.5 StartAngle=4.71239 EndAngle=6.28319
    g7: ArcOfCircle CenterX=7.05 CenterY=9.6 CenterZ=0 NormalX=0 NormalY=0 NormalZ=1 AngleXU=0 Radius=0.5 StartAngle=5e-16 EndAngle=1.5708
    g8: LineSegment StartX=7.55 StartY=4.35 StartZ=0 EndX=7.55 EndY=2.6 EndZ=0
    g9: LineSegment StartX=7.55 StartY=7.85 StartZ=0 EndX=7.55 EndY=9.6 EndZ=0
    g10: LineSegment StartX=7.05 StartY=10.1 StartZ=0 EndX=-16.95 EndY=10.1 EndZ=0
    g11: LineSegment StartX=5.25 StartY=8.75 StartZ=0 EndX=-9.25715 EndY=8.75 EndZ=0
    g12: LineSegment StartX=5.25 StartY=3.45 StartZ=0 EndX=-1.95 EndY=3.45 EndZ=0
    g13: ArcOfCircle CenterX=-14.7544 CenterY=-6.51631 CenterZ=0 NormalX=0 NormalY=0 NormalZ=1 AngleXU=0 Radius=16.2259 StartAngle=0.6614 EndAngle=1.22516
    g14: LineSegment StartX=7.05 StartY=2.1 StartZ=0 EndX=-2.35 EndY=2.1 EndZ=0
    g15: ArcOfCircle CenterX=-14.7544 CenterY=-6.51631 CenterZ=0 NormalX=0 NormalY=0 NormalZ=1 AngleXU=0 Radius=15.1033 StartAngle=0.607104 EndAngle=1.31616
    g16: LineSegment StartX=-16.95 StartY=10.1 StartZ=0 EndX=-16.95 EndY=8.1 EndZ=0
    g17: LineSegment StartX=-16.95 StartY=8.1 StartZ=0 EndX=-10.95 EndY=8.1 EndZ=0
  constraints (46):
    c: Coincident(g0,g-14)
    c: Coincident(g0,g-9)
    c: Coincident(g1,g0)
    c: Coincident(g1,g-10)
    c: Coincident(g2,g-15)
    c: Coincident(g2,g-3)
    c: Coincident(g3,g2)
    c: Coincident(g3,g-4)
    c: Coincident(g4,g3)
    c: Coincident(g4,g-5)
    c: Coincident(g5,g1)
    c: Coincident(g5,g-11)
    c: Tangent(g6,g-12) = -1.5708
    c: Coincident(g6,g-13)
    c: Coincident(g7,g-7)
    c: Tangent(g7,g-6) = -1.5708
    c: Tangent(g4,g-4)
    c: Tangent(g5,g-10)
    c: Coincident(g8,g5)
    c: Coincident(g8,g6)
    c: Coincident(g9,g4)
    c: Coincident(g9,g7)
    c: Coincident(g10,g7)
    c: Coincident(g11,g2)
    c: Horizontal(g11)
    c: Coincident(g12,g0)
    c: Horizontal(g12)
    c: Coincident(g13,g12)
    c: Coincident(g13,g11)
    c: Coincident(g14,g6)
    c: PointOnObject(g14,g-13)
    c: Coincident(g15,g14)
    c: DistanceX(g-13,g14) = 2
    c: DistanceX(g10,g10) = 24
    c: DistanceX(g-18,g10) = 3.6
    c: Coincident(g16,g10)
    c: Vertical(g16)
    c: DistanceY(g16,g16) = 2
    c: Coincident(g17,g16)
    c: Coincident(g17,g15)
    c: Horizontal(g17)
    c: PointOnObject(g10,g-19)
    c: DistanceX(g17,g17) = 6
    c: Coincident(g13,g15)
    c: Tangent(g15,g-20)
    c: DistanceX(g12,g12) = 7.2
FEATURE [PartDesign::Pad] Pad172
  Direction = (0,-1,2e-16)
  Length = 5.6
  Length2 = 10
  Profile = -> Sketch287
  ReferenceAxis = -> Sketch287 [N_Axis]
  Refine = true
  Suppressed = false
  Type = 0
FEATURE [Sketcher::SketchObject] Sketch288
  ArcFitTolerance = 1e-06
  AttachmentSupport = -> [Pad172]
  ExternalGeometry = -> [Pad172]
  FullyConstrained = true
  MakeInternals = false
  MapMode = 5
  Placement = pos=(0,-15.1,0) rot=(0,0.707107,0.707107;3.14159rad)
  sketch-geometry (4):
    g0: LineSegment StartX=1.95 StartY=3.45 StartZ=0 EndX=3.40616 EndY=3.45 EndZ=0
    g1: ArcOfCircle CenterX=14.7544 CenterY=-6.51631 CenterZ=0 NormalX=0 NormalY=0 NormalZ=1 AngleXU=0 Radius=16.2259 StartAngle=2.10797 EndAngle=2.48019
    g2: ArcOfCircle CenterX=14.7544 CenterY=-6.51627 CenterZ=0 NormalX=0 NormalY=0 NormalZ=1 AngleXU=0 Radius=15.1033 StartAngle=2.15285 EndAngle=2.42094
    g3: LineSegment StartX=6.45147 StartY=6.1 StartZ=0 EndX=6.45147 EndY=7.42433 EndZ=0
  constraints (14):
    c: Coincident(g0,g-3)
    c: PointOnObject(g0,g-4)
    c: Horizontal(g0)
    c: PointOnObject(g1,g-3)
    c: PointOnObject(g2,g-4)
    c: Coincident(g1,g0)
    c: Tangent(g1,g-3)
    c: Coincident(g2,g0)
    c: Tangent(g2,g-4)
    c: Coincident(g3,g2)
    c: Coincident(g3,g1)
    c: Vertical(g3)
    c: DistanceY(g-6,g-5) = 8
    c: DistanceY(g-6,g2) = 4
FEATURE [PartDesign::Pocket] Pocket120
  BaseFeature = -> Pad172
  Direction = (0,-1,2e-16)
  Length = 1
  Length2 = 5
  Profile = -> Sketch288
  ReferenceAxis = -> Sketch288 [N_Axis]
  Refine = true
  Suppressed = false
  Type = 0
FEATURE [Sketcher::SketchObject] Sketch289
  ArcFitTolerance = 1e-06
  AttachmentSupport = -> [Pocket120]
  ExternalGeometry = -> [Pocket120]
  FullyConstrained = true
  MakeInternals = false
  MapMode = 5
  Placement = pos=(0,-20.7,0) rot=(1,0,0;1.5708rad)
  sketch-geometry (10):
    g0: ArcOfCircle CenterX=7.05 CenterY=7.85 CenterZ=0 NormalX=0 NormalY=0 NormalZ=1 AngleXU=0 Radius=0.500004 StartAngle=4.7124 EndAngle=6.28318
    g1: ArcOfCircle CenterX=7.05 CenterY=4.35 CenterZ=0 NormalX=0 NormalY=0 NormalZ=1 AngleXU=0 Radius=0.500004 StartAngle=7.39517e-06 EndAngle=1.57079
    g2: LineSegment StartX=7.05 StartY=7.35 StartZ=0 EndX=5.25 EndY=7.35 EndZ=0
    g3: LineSegment StartX=5.25 StartY=7.35 StartZ=0 EndX=5.25 EndY=8.75 EndZ=0
    g4: LineSegment StartX=5.25 StartY=8.75 StartZ=0 EndX=-9.25715 EndY=8.75 EndZ=0
    g5: LineSegment StartX=7.05 StartY=4.85 StartZ=0 EndX=5.25 EndY=4.85 EndZ=0
    g6: LineSegment StartX=5.25 StartY=4.85 StartZ=0 EndX=5.25 EndY=3.45 EndZ=0
    g7: LineSegment StartX=5.25 StartY=3.45 StartZ=0 EndX=-1.95 EndY=3.45 EndZ=0
    g8: ArcOfCircle CenterX=-14.7544 CenterY=-6.51631 CenterZ=0 NormalX=0 NormalY=0 NormalZ=1 AngleXU=0 Radius=16.2259 StartAngle=0.6614 EndAngle=1.22516
    g9: LineSegment StartX=7.55 StartY=7.85 StartZ=0 EndX=7.55 EndY=4.35 EndZ=0
  constraints (21):
    c: Tangent(g0,g-3) = -1.5708
    c: Coincident(g0,g-4)
    c: Tangent(g1,g-11) = -1.5708
    c: Coincident(g1,g-11)
    c: Coincident(g2,g0)
    c: Coincident(g2,g-5)
    c: Coincident(g3,g2)
    c: Coincident(g3,g-6)
    c: Coincident(g4,g3)
    c: Coincident(g4,g-7)
    c: Coincident(g5,g1)
    c: Coincident(g5,g-10)
    c: Coincident(g6,g5)
    c: Coincident(g6,g-9)
    c: Coincident(g7,g6)
    c: Coincident(g7,g-8)
    c: Coincident(g8,g4)
    c: Coincident(g8,g7)
    c: Tangent(g8,g-7)
    c: Coincident(g9,g0)
    c: Coincident(g9,g1)
FEATURE [PartDesign::Pad] Pad173
  BaseFeature = -> Pocket120
  Direction = (0,-1,2e-16)
  Length = 1.5
  Length2 = 10
  Profile = -> Sketch289
  ReferenceAxis = -> Sketch289 [N_Axis]
  Refine = true
  Reversed = true
  Suppressed = false
  Type = 0
FEATURE [Sketcher::SketchObject] Sketch290
  ArcFitTolerance = 1e-06
  AttachmentSupport = -> [Pad173]
  ExternalGeometry = -> [Binder003]
  FullyConstrained = true
  MakeInternals = false
  MapMode = 5
  Placement = pos=(0,-16.1,5.8e-15) rot=(0,0.707107,0.707107;3.14159rad)
  sketch-geometry (1):
    g0: Circle CenterX=2.55 CenterY=6.1 CenterZ=0 NormalX=0 NormalY=0 NormalZ=1 AngleXU=0 Radius=2.25
  constraints (2):
    c: Coincident(g0,g-3)
    c: Diameter(g0) = 4.5
FEATURE [PartDesign::Pad] Pad174
  BaseFeature = -> Pad173
  Direction = (0,1,-2e-16)
  Length = 4
  Length2 = 10
  Profile = -> Sketch290
  ReferenceAxis = -> Sketch290 [N_Axis]
  Refine = true
  Reversed = true
  Suppressed = false
  Type = 0
FEATURE [Sketcher::SketchObject] Sketch291
  ArcFitTolerance = 1e-06
  AttachmentSupport = -> [Pad174]
  ExternalGeometry = -> [Pad174]
  FullyConstrained = true
  MakeInternals = false
  MapMode = 5
  Placement = pos=(-7.1e-15,-16.1,0) rot=(0,0.707107,0.707107;3.14159rad)
  sketch-geometry (1):
    g0: Circle CenterX=2.55 CenterY=6.1 CenterZ=0 NormalX=0 NormalY=0 NormalZ=1 AngleXU=0 Radius=0.75
  constraints (2):
    c: Coincident(g0,g-3)
    c: Radius(g0) = 0.75
FEATURE [PartDesign::Pocket] Pocket121
  BaseFeature = -> Pad174
  Direction = (0,-1,2e-16)
  Length = 3
  Length2 = 5
  Profile = -> Sketch291
  ReferenceAxis = -> Sketch291 [N_Axis]
  Refine = true
  Suppressed = false
  Type = 0
FEATURE [Sketcher::SketchObject] Sketch292
  ArcFitTolerance = 1e-06
  AttachmentSupport = -> [Pocket121]
  ExternalGeometry = -> [Pocket121]
  FullyConstrained = true
  MakeInternals = false
  MapMode = 5
  Placement = pos=(0,2.2e-15,10.1) rot=(0,0,1;0rad)
  sketch-geometry (4):
    g0: LineSegment StartX=-16.95 StartY=-20.7 StartZ=0 EndX=-9.95 EndY=-20.7 EndZ=0
    g1: LineSegment StartX=-9.95 StartY=-20.7 StartZ=0 EndX=-11.95 EndY=-20.9 EndZ=0
    g2: LineSegment StartX=-11.95 StartY=-20.9 StartZ=0 EndX=-16.95 EndY=-20.9 EndZ=0
    g3: LineSegment StartX=-16.95 StartY=-20.7 StartZ=0 EndX=-16.95 EndY=-20.9 EndZ=0
  constraints (11):
    c: Coincident(g0,g-3)
    c: Coincident(g1,g0)
    c: Coincident(g2,g1)
    c: Horizontal(g2)
    c: Coincident(g3,g0)
    c: Coincident(g3,g2)
    c: Vertical(g3)
    c: DistanceY(g3,g3) = 0.2
    c: DistanceX(g2,g2) = 5
    c: PointOnObject(g0,g-3)
    c: DistanceX(g0,g0) = 7
FEATURE [PartDesign::Pad] Pad175
  BaseFeature = -> Pocket121
  Direction = (0,0,1)
  Length = 2
  Length2 = 10
  Profile = -> Sketch292
  ReferenceAxis = -> Sketch292 [N_Axis]
  Refine = true
  Reversed = true
  Suppressed = false
  Type = 0
FEATURE [Sketcher::SketchObject] Sketch293
  ArcFitTolerance = 1e-06
  AttachmentSupport = -> [Pad175]
  ExternalGeometry = -> [Pad175]
  FullyConstrained = true
  MakeInternals = false
  MapMode = 5
  Placement = pos=(0,-20.7,9.7e-15) rot=(1,0,0;1.5708rad)
  sketch-geometry (28):
    g0: LineSegment StartX=4.55 StartY=10.1 StartZ=0 EndX=2.55 EndY=10.1 EndZ=0
    g1: LineSegment StartX=2.55 StartY=10.1 StartZ=0 EndX=2.55 EndY=2.1 EndZ=0
    g2: LineSegment StartX=2.55 StartY=2.1 StartZ=0 EndX=4.55 EndY=2.1 EndZ=0
    g3: LineSegment StartX=4.55 StartY=2.1 StartZ=0 EndX=4.55 EndY=10.1 EndZ=0
    g4: LineSegment StartX=0.55 StartY=10.1 StartZ=0 EndX=-1.45 EndY=10.1 EndZ=0
    g5: LineSegment StartX=-1.45 StartY=10.1 StartZ=0 EndX=-1.45 EndY=2.1 EndZ=0
    g6: LineSegment StartX=-1.45 StartY=2.1 StartZ=0 EndX=0.55 EndY=2.1 EndZ=0
    g7: LineSegment StartX=0.55 StartY=2.1 StartZ=0 EndX=0.55 EndY=10.1 EndZ=0
    g8: LineSegment StartX=-8.95 StartY=10.1 StartZ=0 EndX=-8.95 EndY=7.85585 EndZ=0
    g9: LineSegment StartX=-8.45 StartY=10.1 StartZ=0 EndX=-8.45 EndY=7.64365 EndZ=0
    g10: ArcOfCircle CenterX=-14.7544 CenterY=-6.51631 CenterZ=0 NormalX=0 NormalY=0 NormalZ=1 AngleXU=0 Radius=15.5 StartAngle=1.15192 EndAngle=1.18696
    g11: LineSegment StartX=-8.95 StartY=10.1 StartZ=0 EndX=-8.45 EndY=10.1 EndZ=0
    g12: LineSegment StartX=-7.45 StartY=10.1 StartZ=0 EndX=-7.45 EndY=7.15467 EndZ=0
    g13: LineSegment StartX=-6.95 StartY=10.1 StartZ=0 EndX=-6.95 EndY=6.87552 EndZ=0
    g14: LineSegment StartX=-7.45 StartY=10.1 StartZ=0 EndX=-6.95 EndY=10.1 EndZ=0
    g15: LineSegment StartX=-5.95 StartY=10.1 StartZ=0 EndX=-5.95 EndY=6.24035 EndZ=0
    g16: LineSegment StartX=-5.45 StartY=10.1 StartZ=0 EndX=-5.45 EndY=5.88038 EndZ=0
    g17: LineSegment StartX=-5.95 StartY=10.1 StartZ=0 EndX=-5.45 EndY=10.1 EndZ=0
    g18: ArcOfCircle CenterX=-14.7544 CenterY=-6.51631 CenterZ=0 NormalX=0 NormalY=0 NormalZ=1 AngleXU=0 Radius=15.5 StartAngle=1.04314 EndAngle=1.08009
    g19: ArcOfCircle CenterX=-14.7544 CenterY=-6.51631 CenterZ=0 NormalX=0 NormalY=0 NormalZ=1 AngleXU=0 Radius=15.5 StartAngle=0.92694 EndAngle=0.966691
    g20: LineSegment StartX=-4.45 StartY=10.1 StartZ=0 EndX=-4.45 EndY=5.06252 EndZ=0
    g21: LineSegment StartX=-3.95 StartY=10.1 StartZ=0 EndX=-3.95 EndY=4.59741 EndZ=0
    g22: LineSegment StartX=-3.95 StartY=10.1 StartZ=0 EndX=-4.45 EndY=10.1 EndZ=0
    g23: ArcOfCircle CenterX=-14.7544 CenterY=-6.51631 CenterZ=0 NormalX=0 NormalY=0 NormalZ=1 AngleXU=0 Radius=15.5 StartAngle=0.79951 EndAngle=0.84357
    g24: LineSegment StartX=-2.95 StartY=10.1 StartZ=0 EndX=-2.95 EndY=3.52889 EndZ=0
    g25: LineSegment StartX=-2.45 StartY=10.1 StartZ=0 EndX=-2.45 EndY=2.9098 EndZ=0
    g26: LineSegment StartX=-2.45 StartY=10.1 StartZ=0 EndX=-2.95 EndY=10.1 EndZ=0
    g27: ArcOfCircle CenterX=-14.7544 CenterY=-6.51631 CenterZ=0 NormalX=0 NormalY=0 NormalZ=1 AngleXU=0 Radius=15.5 StartAngle=0.653711 EndAngle=0.705057
  constraints (84):
    c: Coincident(g0,g1)
    c: Coincident(g1,g2)
    c: Coincident(g2,g3)
    c: Coincident(g3,g0)
    c: Horizontal(g0)
    c: Horizontal(g2)
    c: Vertical(g1)
    c: Vertical(g3)
    c: PointOnObject(g0,g-3)
    c: PointOnObject(g1,g-4)
    c: Coincident(g4,g5)
    c: Coincident(g5,g6)
    c: Coincident(g6,g7)
    c: Coincident(g7,g4)
    c: Horizontal(g4)
    c: Horizontal(g6)
    c: Vertical(g5)
    c: Vertical(g7)
    c: PointOnObject(g4,g-3)
    c: PointOnObject(g5,g-4)
    c: PointOnObject(g8,g-3)
    c: Vertical(g8)
    c: PointOnObject(g9,g-3)
    c: Vertical(g9)
    c: Coincident(g10,g8)
    c: Coincident(g10,g9)
    c: Coincident(g11,g8)
    c: Coincident(g11,g9)
    c: PointOnObject(g12,g-3)
    c: Vertical(g12)
    c: PointOnObject(g13,g-3)
    c: Vertical(g13)
    c: Coincident(g14,g12)
    c: Coincident(g14,g13)
    c: PointOnObject(g15,g-3)
    c: Vertical(g15)
    c: PointOnObject(g16,g-3)
    c: Vertical(g16)
    c: Coincident(g17,g15)
    c: Coincident(g17,g16)
    c: Coincident(g18,g12)
    c: Coincident(g18,g13)
    c: Coincident(g19,g15)
    c: Coincident(g19,g16)
    c: PointOnObject(g20,g-3)
    c: Vertical(g20)
    c: PointOnObject(g21,g-3)
    c: Vertical(g21)
    c: Coincident(g22,g21)
    c: Coincident(g22,g20)
    c: Coincident(g23,g20)
    c: Coincident(g23,g21)
    c: PointOnObject(g24,g-3)
    c: Vertical(g24)
    c: Vertical(g25)
    c: Coincident(g26,g25)
    c: Coincident(g26,g24)
    c: Coincident(g27,g24)
    c: Coincident(g27,g25)
    c: Coincident(g10,g-5)
    c: Coincident(g18,g10)
    c: DistanceX(g11,g11) = 0.5
    c: DistanceX(g14,g14) = 0.5
    c: DistanceX(g17,g17) = 0.5
    c: DistanceX(g22,g22) = 0.5
    c: DistanceX(g26,g26) = 0.5
    c: DistanceX(g9,g12) = 1
    c: DistanceX(g13,g15) = 1
    c: DistanceX(g16,g20) = 1
    c: DistanceX(g21,g24) = 1
    c: Coincident(g19,g10)
    c: Coincident(g23,g10)
    c: Coincident(g27,g10)
    c: DistanceX(g-6,g8) = 1
    c: PointOnObject(g25,g-3)
    c: Radius(g10) = 15.5
    c: Radius(g18) = 15.5
    c: Radius(g27) = 15.5
    c: Radius(g23) = 15.5
    c: Radius(g19) = 15.5
    c: DistanceX(g4,g4) = 2
    c: DistanceX(g0,g0) = 2
    c: DistanceX(g2,g-9) = 3
    c: DistanceX(g6,g1) = 2
FEATURE [PartDesign::Pocket] Pocket122
  BaseFeature = -> Pad175
  Direction = (0,1,-2e-16)
  Length = 0.5
  Length2 = 5
  Profile = -> Sketch293
  ReferenceAxis = -> Sketch293 [N_Axis]
  Refine = true
  Suppressed = false
  Type = 0
FEATURE [Sketcher::SketchObject] Sketch294
  ArcFitTolerance = 1e-06
  AttachmentSupport = -> [Pocket122]
  ExternalGeometry = -> [Pocket122]
  FullyConstrained = true
  MakeInternals = false
  MapMode = 5
  Placement = pos=(0,5e-16,2.1) rot=(1,0,0;3.14159rad)
  sketch-geometry (8):
    g0: LineSegment StartX=-1.45 StartY=20.2 StartZ=0 EndX=-1.45 EndY=15.1 EndZ=0
    g1: LineSegment StartX=-1.45 StartY=15.1 StartZ=0 EndX=0.55 EndY=15.1 EndZ=0
    g2: LineSegment StartX=0.55 StartY=15.1 StartZ=0 EndX=0.55 EndY=20.2 EndZ=0
    g3: LineSegment StartX=0.55 StartY=20.2 StartZ=0 EndX=-1.45 EndY=20.2 EndZ=0
    g4: LineSegment StartX=2.55 StartY=20.2 StartZ=0 EndX=2.55 EndY=15.1 EndZ=0
    g5: LineSegment StartX=2.55 StartY=15.1 StartZ=0 EndX=4.55 EndY=15.1 EndZ=0
    g6: LineSegment StartX=4.55 StartY=15.1 StartZ=0 EndX=4.55 EndY=20.2 EndZ=0
    g7: LineSegment StartX=4.55 StartY=20.2 StartZ=0 EndX=2.55 EndY=20.2 EndZ=0
  constraints (20):
    c: Coincident(g0,g1)
    c: Coincident(g1,g2)
    c: Coincident(g2,g3)
    c: Coincident(g3,g0)
    c: Vertical(g0)
    c: Vertical(g2)
    c: Horizontal(g1)
    c: Coincident(g0,g-5)
    c: PointOnObject(g1,g-3)
    c: Coincident(g4,g5)
    c: Coincident(g5,g6)
    c: Coincident(g6,g7)
    c: Coincident(g7,g4)
    c: Vertical(g4)
    c: Vertical(g6)
    c: Horizontal(g5)
    c: Coincident(g4,g-4)
    c: PointOnObject(g5,g-3)
    c: Coincident(g2,g-5)
    c: Coincident(g6,g-4)
FEATURE [PartDesign::Pocket] Pocket123
  BaseFeature = -> Pocket122
  Direction = (0,0,1)
  Length = 0.5
  Length2 = 5
  Profile = -> Sketch294
  ReferenceAxis = -> Sketch294 [N_Axis]
  Refine = true
  Suppressed = false
  Type = 0
FEATURE [Sketcher::SketchObject] Sketch295
  ArcFitTolerance = 1e-06
  AttachmentSupport = -> [Pocket123]
  ExternalGeometry = -> [Pocket123]
  FullyConstrained = true
  MakeInternals = false
  MapMode = 5
  Placement = pos=(0,0,10.1) rot=(0,0,1;0rad)
  sketch-geometry (8):
    g0: LineSegment StartX=0.55 StartY=-20.2 StartZ=0 EndX=0.55 EndY=-15.1 EndZ=0
    g1: LineSegment StartX=0.55 StartY=-15.1 StartZ=0 EndX=-1.45 EndY=-15.1 EndZ=0
    g2: LineSegment StartX=-1.45 StartY=-15.1 StartZ=0 EndX=-1.45 EndY=-20.2 EndZ=0
    g3: LineSegment StartX=-1.45 StartY=-20.2 StartZ=0 EndX=0.55 EndY=-20.2 EndZ=0
    g4: LineSegment StartX=4.55 StartY=-20.2 StartZ=0 EndX=4.55 EndY=-15.1 EndZ=0
    g5: LineSegment StartX=4.55 StartY=-15.1 StartZ=0 EndX=2.55 EndY=-15.1 EndZ=0
    g6: LineSegment StartX=2.55 StartY=-15.1 StartZ=0 EndX=2.55 EndY=-20.2 EndZ=0
    g7: LineSegment StartX=2.55 StartY=-20.2 StartZ=0 EndX=4.55 EndY=-20.2 EndZ=0
  constraints (20):
    c: Coincident(g0,g1)
    c: Coincident(g1,g2)
    c: Coincident(g2,g3)
    c: Coincident(g3,g0)
    c: Vertical(g0)
    c: Vertical(g2)
    c: Horizontal(g1)
    c: Coincident(g0,g-4)
    c: PointOnObject(g1,g-5)
    c: Coincident(g4,g5)
    c: Coincident(g5,g6)
    c: Coincident(g6,g7)
    c: Coincident(g7,g4)
    c: Vertical(g4)
    c: Vertical(g6)
    c: Horizontal(g5)
    c: Coincident(g4,g-3)
    c: PointOnObject(g5,g-5)
    c: Coincident(g2,g-4)
    c: Coincident(g6,g-3)
FEATURE [PartDesign::Pocket] Pocket124
  BaseFeature = -> Pocket123
  Direction = (0,0,-1)
  Length = 0.5
  Length2 = 5
  Profile = -> Sketch295
  ReferenceAxis = -> Sketch295 [N_Axis]
  Refine = true
  Suppressed = false
  Type = 0
FEATURE [Sketcher::SketchObject] Sketch302
  ArcFitTolerance = 1e-06
  AttachmentSupport = -> [Pocket124]
  ExternalGeometry = -> [Pocket124]
  FullyConstrained = true
  MakeInternals = false
  MapMode = 5
  Placement = pos=(0,-15.1,0) rot=(0,0.707107,0.707107;3.14159rad)
  sketch-geometry (12):
    g0: LineSegment StartX=-5.25 StartY=4.85 StartZ=0 EndX=-5.25 EndY=4.975 EndZ=0
    g1: LineSegment StartX=-7.55 StartY=4.35 StartZ=0 EndX=-7.55 EndY=4.475 EndZ=0
    g2: ArcOfCircle CenterX=-7.05 CenterY=4.35 CenterZ=0 NormalX=0 NormalY=0 NormalZ=1 AngleXU=0 Radius=0.500004 StartAngle=1.5708 EndAngle=3.14159
    g3: LineSegment StartX=-7.05 StartY=4.85 StartZ=0 EndX=-5.25 EndY=4.85 EndZ=0
    g4: LineSegment StartX=-5.25 StartY=4.975 StartZ=0 EndX=-7.05 EndY=4.975 EndZ=0
    g5: ArcOfCircle CenterX=-7.05 CenterY=4.475 CenterZ=0 NormalX=0 NormalY=0 NormalZ=1 AngleXU=0 Radius=0.5 StartAngle=1.5708 EndAngle=3.14159
    g6: LineSegment StartX=-5.25 StartY=7.35 StartZ=0 EndX=-5.25 EndY=7.225 EndZ=0
    g7: LineSegment StartX=-7.55 StartY=7.85 StartZ=0 EndX=-7.55 EndY=7.725 EndZ=0
    g8: ArcOfCircle CenterX=-7.05 CenterY=7.85 CenterZ=0 NormalX=0 NormalY=0 NormalZ=1 AngleXU=0 Radius=0.500004 StartAngle=3.1416 EndAngle=4.71238
    g9: LineSegment StartX=-7.05 StartY=7.35 StartZ=0 EndX=-5.25 EndY=7.35 EndZ=0
    g10: ArcOfCircle CenterX=-7.05 CenterY=7.725 CenterZ=0 NormalX=0 NormalY=0 NormalZ=1 AngleXU=0 Radius=0.5 StartAngle=3.14159 EndAngle=4.71239
    g11: LineSegment StartX=-7.05 StartY=7.225 StartZ=0 EndX=-5.25 EndY=7.225 EndZ=0
  constraints (33):
    c: Coincident(g0,g-8)
    c: Coincident(g1,g-9)
    c: PointOnObject(g1,g-9)
    c: Coincident(g2,g1)
    c: Coincident(g2,g-7)
    c: Tangent(g2,g-6)
    c: Coincident(g3,g2)
    c: Coincident(g3,g0)
    c: Vertical(g0)
    c: Coincident(g4,g0)
    c: Horizontal(g4)
    c: Coincident(g5,g1)
    c: Coincident(g5,g4)
    c: DistanceY(g0,g0) = 0.125
    c: DistanceY(g1,g1) = 0.125
    c: DistanceX(g2,g4) = 0
    c: Radius(g5) = 0.5
    c: Coincident(g6,g-4)
    c: Vertical(g6)
    c: Coincident(g7,g-9)
    c: PointOnObject(g7,g-9)
    c: Coincident(g8,g7)
    c: Tangent(g8,g-5) = -1.5708
    c: Coincident(g9,g8)
    c: Coincident(g9,g6)
    c: Coincident(g10,g7)
    c: Coincident(g11,g10)
    c: Coincident(g11,g6)
    c: Horizontal(g11)
    c: DistanceY(g6,g6) = 0.125
    c: DistanceY(g7,g7) = 0.125
    c: Radius(g10) = 0.5
    c: DistanceX(g10,g8) = 0
FEATURE [PartDesign::Pad] Pad179
  BaseFeature = -> Pocket124
  Direction = (0,1,-2e-16)
  Length = 4.15
  Length2 = 10
  Profile = -> Sketch302
  ReferenceAxis = -> Sketch302 [N_Axis]
  Refine = true
  Reversed = true
  Suppressed = false
  Type = 0
FEATURE [PartDesign::Body] Body010  label="Rigt_Outer_Arm"
  AllowCompound = false
  Group = -> [Binder003,Sketch287,Pad172,Sketch288,Pocket120,Sketch289,Pad173,Sketch290,Pad174,Sketch291,Pocket121,Sketch292,Pad175,Sketch293,Pocket122,Sketch294,Pocket123,Sketch295,Pocket124,Sketch302,Pad179]
  Origin = -> Origin010
  Tip = -> Pad179
COMPONENT P19 — geometry summary ("Tire6"; no construction recipe available for this part):
  bounding box: 18.0 x 18.0 x 5.5 mm
  tessellated surface: 8,474 triangles
  volume: 995 mm^3 (56% of its bounding box)
  symmetry: 4-fold rotationally symmetric about the y axis; mirror-symmetric across its x mid-plane, z mid-plane
COMPONENT P20 — geometry summary ("Head"; no construction recipe available for this part):
  bounding box: 13.6 x 12.6 x 7.9 mm
  tessellated surface: 5,480 triangles
  volume: 371 mm^3 (27% of its bounding box)
  symmetry: mirror-symmetric across its y mid-plane
PROVENANCE & LICENSES
A FreeCAD (.FCStd) document from a public repository crawl; recipes are the document's own serialized feature recipes (and, for linked parts, companion documents' recipes).
License: as declared in the source repository (recorded in the dataset sidecar).
